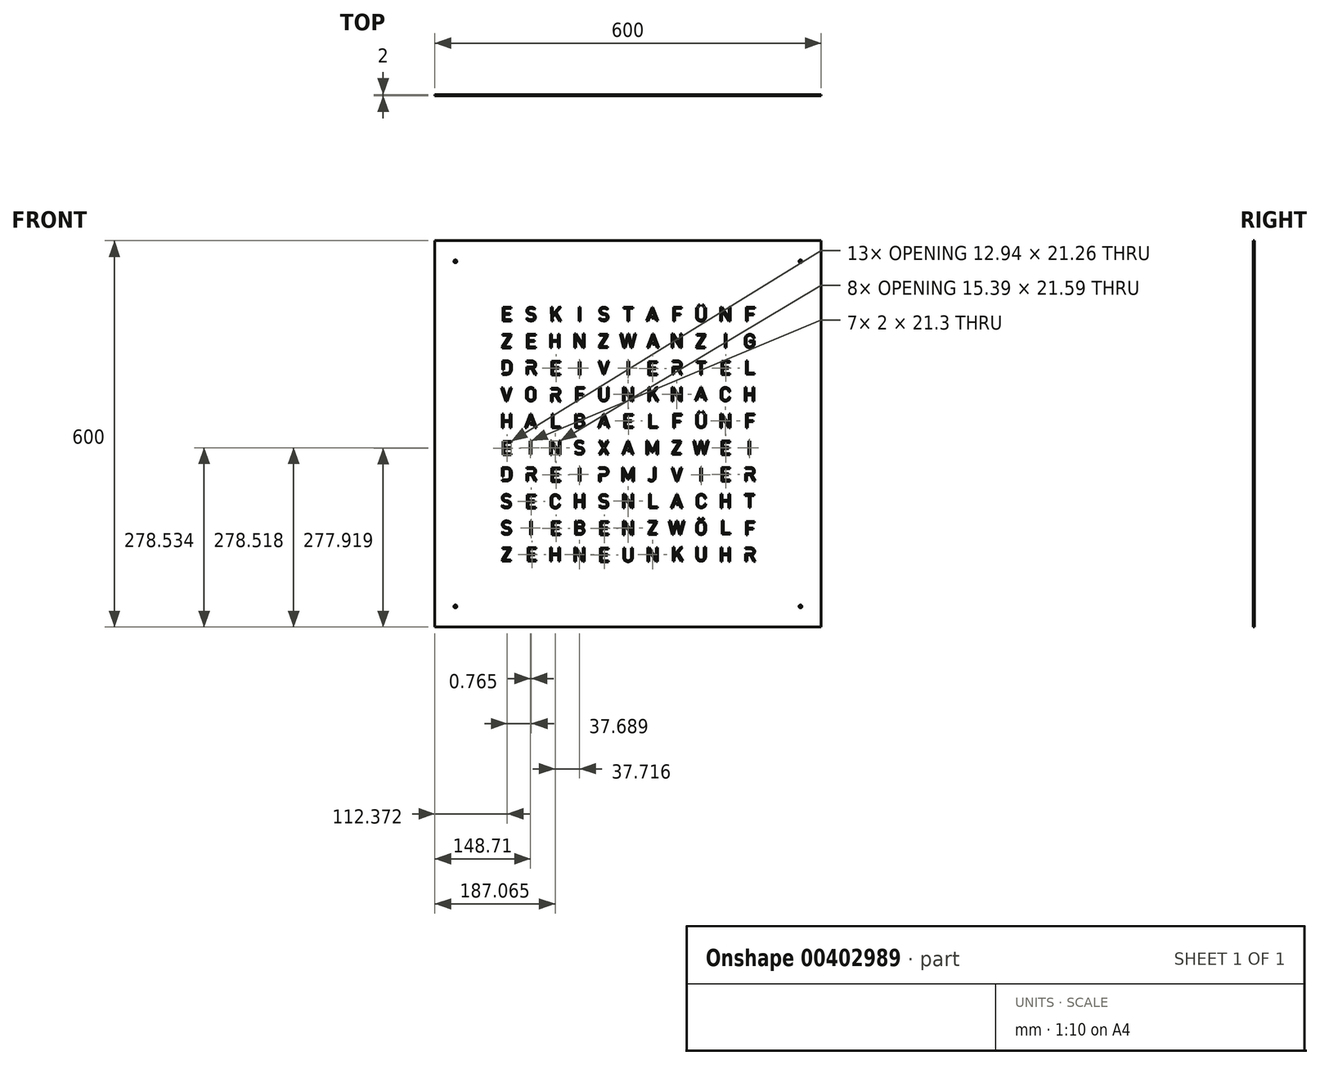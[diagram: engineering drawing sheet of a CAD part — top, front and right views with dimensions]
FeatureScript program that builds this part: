
annotation { "Feature Type Name" : "Feature", "Feature Type Description" : "" }
export const myFeature = defineFeature(function(context is Context, id is Id, definition is map)
    precondition{}
    {
        {
            var Q0;
            Q0=qCreatedBy(makeId("Front.planeOp"),FACE);
            var sketch = newSketch(context, id + "F0", { "sketchPlane" : qUnion([Q0])});
            skLineSegment(sketch, "E0.bottom", {"start": v(-458.3, 400.46) * mm, "end": v(141.7, 400.46) * mm});
            skLineSegment(sketch, "E0.top", {"start": v(-458.3, -199.54) * mm, "end": v(141.7, -199.54) * mm});
            skLineSegment(sketch, "E0.left", {"start": v(-458.3, 400.46) * mm, "end": v(-458.3, -199.54) * mm});
            skLineSegment(sketch, "E0.right", {"start": v(141.7, 400.46) * mm, "end": v(141.7, -199.54) * mm});
            skLineSegment(sketch, "E1", {"start": v(-354.69, 171.84) * mm, "end": v(-347.74, 151.15) * mm});
            skLineSegment(sketch, "E2", {"start": v(-347.74, 151.15) * mm, "end": v(-345.77, 151.15) * mm});
            skLineSegment(sketch, "E3", {"start": v(-345.77, 151.15) * mm, "end": v(-338.81, 171.84) * mm});
            skLineSegment(sketch, "E4", {"start": v(-338.81, 171.84) * mm, "end": v(-340.92, 171.84) * mm});
            skLineSegment(sketch, "E5", {"start": v(-340.92, 171.84) * mm, "end": v(-346.75, 154.5) * mm});
            skPoint(sketch, "E5.endSnap0", {"position": v(-346.75, 151.15) * mm});
            skLineSegment(sketch, "E6", {"start": v(-346.75, 154.5) * mm, "end": v(-352.58, 171.84) * mm});
            skLineSegment(sketch, "E7", {"start": v(-352.58, 171.84) * mm, "end": v(-354.69, 171.84) * mm});
            skArc(sketch, "E8", {"start": v(-268.37, 161.99) * mm, "mid": v(-265.4, 166.18) * mm, "end": v(-269.23, 169.6) * mm});
            skArc(sketch, "E9", {"start": v(-268.17, 159.99) * mm, "mid": v(-263.4, 166.28) * mm, "end": v(-269.23, 171.6) * mm});
            skLineSegment(sketch, "E10", {"start": v(-269.23, 171.6) * mm, "end": v(-277.66, 171.6) * mm});
            skLineSegment(sketch, "E11", {"start": v(-277.66, 171.6) * mm, "end": v(-277.66, 169.6) * mm});
            skLineSegment(sketch, "E12", {"start": v(-277.66, 169.6) * mm, "end": v(-269.23, 169.6) * mm});
            skLineSegment(sketch, "E13", {"start": v(-268.37, 161.99) * mm, "end": v(-277.66, 161.99) * mm});
            skLineSegment(sketch, "E14", {"start": v(-277.66, 161.99) * mm, "end": v(-277.66, 150.6) * mm});
            skLineSegment(sketch, "E15", {"start": v(-277.66, 150.6) * mm, "end": v(-275.66, 150.6) * mm});
            skLineSegment(sketch, "E16", {"start": v(-275.66, 150.6) * mm, "end": v(-275.66, 159.99) * mm});
            skLineSegment(sketch, "E17", {"start": v(-275.66, 159.99) * mm, "end": v(-270.17, 159.99) * mm});
            skLineSegment(sketch, "E18", {"start": v(-270.17, 159.99) * mm, "end": v(-264.9, 150.46) * mm});
            skLineSegment(sketch, "E19", {"start": v(-264.9, 150.46) * mm, "end": v(-262.62, 150.46) * mm});
            skLineSegment(sketch, "E20", {"start": v(-262.62, 150.46) * mm, "end": v(-268.17, 159.99) * mm});
            skLineSegment(sketch, "E21", {"start": v(-314.37, 157.95) * mm, "end": v(-314.37, 165.71) * mm});
            skLineSegment(sketch, "E22", {"start": v(-303.94, 165.71) * mm, "end": v(-303.94, 157.95) * mm});
            skArc(sketch, "E23", {"start": v(-314.37, 165.71) * mm, "mid": v(-311.31, 170.45) * mm, "end": v(-305.73, 169.61) * mm});
            skLineSegment(sketch, "E24", {"start": v(-316.37, 165.71) * mm, "end": v(-316.37, 157.95) * mm});
            skLineSegment(sketch, "E25", {"start": v(-301.94, 165.71) * mm, "end": v(-301.94, 157.95) * mm});
            skArc(sketch, "E26", {"start": v(-316.37, 165.71) * mm, "mid": v(-312.26, 172.13) * mm, "end": v(-304.71, 171.08) * mm});
            skArc(sketch, "E27", {"start": v(-301.94, 165.71) * mm, "mid": v(-302.34, 167.92) * mm, "end": v(-303.48, 169.85) * mm});
            skArc(sketch, "E28", {"start": v(-303.94, 165.71) * mm, "mid": v(-304.14, 167.02) * mm, "end": v(-304.71, 168.22) * mm});
            skArc(sketch, "E29", {"start": v(-301.94, 157.95) * mm, "mid": v(-306.07, 151.6) * mm, "end": v(-313.54, 152.82) * mm});
            skArc(sketch, "E30", {"start": v(-303.94, 157.95) * mm, "mid": v(-307.03, 153.38) * mm, "end": v(-312.42, 154.52) * mm});
            skArc(sketch, "E31", {"start": v(-316.37, 157.95) * mm, "mid": v(-315.98, 155.78) * mm, "end": v(-314.87, 153.88) * mm});
            skArc(sketch, "E32", {"start": v(-314.37, 157.95) * mm, "mid": v(-314.19, 156.7) * mm, "end": v(-313.65, 155.57) * mm});
            skLineSegment(sketch, "E33", {"start": v(-305.73, 169.61) * mm, "end": v(-304.71, 171.08) * mm});
            skLineSegment(sketch, "E34", {"start": v(-304.71, 168.22) * mm, "end": v(-303.48, 169.85) * mm});
            skLineSegment(sketch, "E35", {"start": v(-313.65, 155.57) * mm, "end": v(-314.87, 153.88) * mm});
            skLineSegment(sketch, "E36", {"start": v(-312.42, 154.52) * mm, "end": v(-313.54, 152.82) * mm});
            skLineSegment(sketch, "E37", {"start": v(-353.9, 109.8) * mm, "end": v(-353.9, 131.18) * mm});
            skLineSegment(sketch, "E38", {"start": v(-353.9, 131.18) * mm, "end": v(-351.9, 131.18) * mm});
            skLineSegment(sketch, "E39", {"start": v(-351.9, 131.18) * mm, "end": v(-351.9, 121.51) * mm});
            skLineSegment(sketch, "E40", {"start": v(-351.9, 121.51) * mm, "end": v(-341.7, 121.51) * mm});
            skLineSegment(sketch, "E41", {"start": v(-341.7, 121.51) * mm, "end": v(-341.7, 131.18) * mm});
            skLineSegment(sketch, "E42", {"start": v(-341.7, 131.18) * mm, "end": v(-339.7, 131.18) * mm});
            skLineSegment(sketch, "E43", {"start": v(-339.7, 131.18) * mm, "end": v(-339.7, 109.8) * mm});
            skLineSegment(sketch, "E44", {"start": v(-339.7, 109.8) * mm, "end": v(-341.7, 109.8) * mm});
            skLineSegment(sketch, "E45", {"start": v(-341.7, 109.8) * mm, "end": v(-341.7, 119.51) * mm});
            skLineSegment(sketch, "E46", {"start": v(-341.7, 119.51) * mm, "end": v(-351.9, 119.51) * mm});
            skLineSegment(sketch, "E47", {"start": v(-351.9, 119.51) * mm, "end": v(-351.9, 109.8) * mm});
            skLineSegment(sketch, "E48", {"start": v(-351.9, 109.8) * mm, "end": v(-353.9, 109.8) * mm});
            skLineSegment(sketch, "E49", {"start": v(-317.92, 109.8) * mm, "end": v(-309.5, 131.18) * mm});
            skLineSegment(sketch, "E50", {"start": v(-309.5, 131.18) * mm, "end": v(-308.57, 131.18) * mm});
            skLineSegment(sketch, "E51", {"start": v(-308.57, 131.18) * mm, "end": v(-300.43, 109.8) * mm});
            skLineSegment(sketch, "E52", {"start": v(-300.43, 109.8) * mm, "end": v(-302.67, 109.8) * mm});
            skLineSegment(sketch, "E53", {"start": v(-302.67, 109.8) * mm, "end": v(-304.7, 115.11) * mm});
            skLineSegment(sketch, "E54", {"start": v(-304.7, 115.11) * mm, "end": v(-309.74, 115.11) * mm});
            skLineSegment(sketch, "E55", {"start": v(-309.74, 115.11) * mm, "end": v(-309.74, 117.11) * mm});
            skLineSegment(sketch, "E56", {"start": v(-309.74, 117.11) * mm, "end": v(-305.35, 117.11) * mm});
            skLineSegment(sketch, "E57", {"start": v(-305.35, 117.11) * mm, "end": v(-309.06, 126.85) * mm});
            skLineSegment(sketch, "E58", {"start": v(-309.06, 126.85) * mm, "end": v(-315.77, 109.8) * mm});
            skLineSegment(sketch, "E59", {"start": v(-315.77, 109.8) * mm, "end": v(-317.92, 109.8) * mm});
            skLineSegment(sketch, "E60", {"start": v(-276.46, 109.8) * mm, "end": v(-263.54, 109.8) * mm});
            skLineSegment(sketch, "E61", {"start": v(-263.54, 109.8) * mm, "end": v(-263.54, 111.8) * mm});
            skLineSegment(sketch, "E62", {"start": v(-263.54, 111.8) * mm, "end": v(-274.46, 111.8) * mm});
            skLineSegment(sketch, "E63", {"start": v(-274.46, 111.8) * mm, "end": v(-274.46, 131.18) * mm});
            skLineSegment(sketch, "E64", {"start": v(-274.46, 131.18) * mm, "end": v(-276.46, 131.18) * mm});
            skLineSegment(sketch, "E65", {"start": v(-276.46, 131.18) * mm, "end": v(-276.46, 109.8) * mm});
            skLineSegment(sketch, "E66", {"start": v(-239, 151.18) * mm, "end": v(-239, 172.67) * mm});
            skLineSegment(sketch, "E67", {"start": v(-239, 172.67) * mm, "end": v(-225.94, 172.67) * mm});
            skLineSegment(sketch, "E68", {"start": v(-225.94, 172.67) * mm, "end": v(-225.94, 170.67) * mm});
            skLineSegment(sketch, "E69", {"start": v(-225.94, 170.67) * mm, "end": v(-237, 170.67) * mm});
            skLineSegment(sketch, "E70", {"start": v(-237, 170.67) * mm, "end": v(-237, 162.42) * mm});
            skLineSegment(sketch, "E71", {"start": v(-237, 162.42) * mm, "end": v(-227.82, 162.42) * mm});
            skLineSegment(sketch, "E72", {"start": v(-227.82, 162.42) * mm, "end": v(-227.82, 160.42) * mm});
            skLineSegment(sketch, "E73", {"start": v(-227.82, 160.42) * mm, "end": v(-237, 160.42) * mm});
            skLineSegment(sketch, "E74", {"start": v(-237, 160.42) * mm, "end": v(-237, 151.18) * mm});
            skLineSegment(sketch, "E75", {"start": v(-237, 151.18) * mm, "end": v(-239, 151.18) * mm});
            skLineSegment(sketch, "E76", {"start": v(-202.89, 172.67) * mm, "end": v(-202.89, 157.96) * mm});
            skLineSegment(sketch, "E77", {"start": v(-200.89, 172.67) * mm, "end": v(-200.89, 157.96) * mm});
            skLineSegment(sketch, "E78", {"start": v(-202.89, 172.67) * mm, "end": v(-200.89, 172.67) * mm});
            skLineSegment(sketch, "E79", {"start": v(-190.7, 172.67) * mm, "end": v(-190.7, 157.96) * mm});
            skLineSegment(sketch, "E80", {"start": v(-188.7, 172.67) * mm, "end": v(-188.7, 157.96) * mm});
            skLineSegment(sketch, "E81", {"start": v(-190.7, 172.67) * mm, "end": v(-188.7, 172.67) * mm});
            skArc(sketch, "E82", {"start": v(-200.89, 157.96) * mm, "mid": v(-195.8, 152.87) * mm, "end": v(-190.7, 157.96) * mm});
            skArc(sketch, "E83", {"start": v(-202.89, 157.96) * mm, "mid": v(-195.8, 150.87) * mm, "end": v(-188.7, 157.96) * mm});
            skLineSegment(sketch, "E84", {"start": v(-165.7, 172.67) * mm, "end": v(-165.7, 151.08) * mm});
            skLineSegment(sketch, "E85", {"start": v(-165.7, 151.08) * mm, "end": v(-163.7, 151.08) * mm});
            skLineSegment(sketch, "E86", {"start": v(-163.7, 151.08) * mm, "end": v(-163.7, 168.95) * mm});
            skLineSegment(sketch, "E87", {"start": v(-163.7, 168.95) * mm, "end": v(-152.3, 151.08) * mm});
            skLineSegment(sketch, "E88", {"start": v(-152.3, 151.08) * mm, "end": v(-150.3, 151.08) * mm});
            skLineSegment(sketch, "E89", {"start": v(-150.3, 151.08) * mm, "end": v(-150.3, 172.67) * mm});
            skLineSegment(sketch, "E90", {"start": v(-150.3, 172.67) * mm, "end": v(-152.3, 172.67) * mm});
            skLineSegment(sketch, "E91", {"start": v(-152.3, 172.67) * mm, "end": v(-152.3, 154.8) * mm});
            skLineSegment(sketch, "E92", {"start": v(-152.3, 154.8) * mm, "end": v(-163.7, 172.67) * mm});
            skLineSegment(sketch, "E93", {"start": v(-163.7, 172.67) * mm, "end": v(-165.7, 172.67) * mm});
            skLineSegment(sketch, "E94", {"start": v(-126.4, 151.08) * mm, "end": v(-126.4, 172.67) * mm});
            skLineSegment(sketch, "E95", {"start": v(-126.4, 172.67) * mm, "end": v(-124.4, 172.67) * mm});
            skLineSegment(sketch, "E96", {"start": v(-124.4, 172.67) * mm, "end": v(-124.4, 160.57) * mm});
            skLineSegment(sketch, "E97", {"start": v(-124.4, 160.57) * mm, "end": v(-114.36, 172.67) * mm});
            skLineSegment(sketch, "E98", {"start": v(-114.36, 172.67) * mm, "end": v(-111.76, 172.67) * mm});
            skLineSegment(sketch, "E99", {"start": v(-111.76, 172.67) * mm, "end": v(-118.9, 164.06) * mm});
            skLineSegment(sketch, "E100", {"start": v(-118.9, 164.06) * mm, "end": v(-111.2, 151.08) * mm});
            skLineSegment(sketch, "E101", {"start": v(-111.2, 151.08) * mm, "end": v(-113.53, 151.08) * mm});
            skLineSegment(sketch, "E102", {"start": v(-113.53, 151.08) * mm, "end": v(-120.18, 162.28) * mm});
            skLineSegment(sketch, "E103", {"start": v(-120.18, 162.28) * mm, "end": v(-124.4, 157.19) * mm});
            skLineSegment(sketch, "E104", {"start": v(-124.4, 157.19) * mm, "end": v(-124.4, 151.08) * mm});
            skLineSegment(sketch, "E105", {"start": v(-124.4, 151.08) * mm, "end": v(-126.4, 151.08) * mm});
            skLineSegment(sketch, "E106", {"start": v(-12.14, 165.54) * mm, "end": v(-12.14, 158.4) * mm});
            skLineSegment(sketch, "E107", {"start": v(-14.14, 158.4) * mm, "end": v(-14.14, 165.54) * mm});
            skArc(sketch, "E108", {"start": v(-12.14, 165.54) * mm, "mid": v(-7.1, 170.78) * mm, "end": v(-1.67, 165.93) * mm});
            skArc(sketch, "E109", {"start": v(-14.14, 165.54) * mm, "mid": v(-7.1, 172.78) * mm, "end": v(0.33, 165.93) * mm});
            skArc(sketch, "E110", {"start": v(-12.14, 158.4) * mm, "mid": v(-7.2, 153.16) * mm, "end": v(-1.67, 157.75) * mm});
            skArc(sketch, "E111", {"start": v(-14.14, 158.4) * mm, "mid": v(-7.21, 151.16) * mm, "end": v(0.33, 157.75) * mm});
            skLineSegment(sketch, "E112", {"start": v(-1.67, 157.75) * mm, "end": v(0.33, 157.75) * mm});
            skLineSegment(sketch, "E113", {"start": v(-1.67, 165.93) * mm, "end": v(0.33, 165.93) * mm});
            skLineSegment(sketch, "E114", {"start": v(-163.64, 130.95) * mm, "end": v(-150.7, 130.95) * mm});
            skLineSegment(sketch, "E115", {"start": v(-150.7, 130.95) * mm, "end": v(-150.7, 128.95) * mm});
            skLineSegment(sketch, "E116", {"start": v(-150.7, 128.95) * mm, "end": v(-161.64, 128.95) * mm});
            skLineSegment(sketch, "E117", {"start": v(-161.64, 128.95) * mm, "end": v(-161.64, 121.44) * mm});
            skLineSegment(sketch, "E118", {"start": v(-161.64, 121.44) * mm, "end": v(-152.42, 121.44) * mm});
            skLineSegment(sketch, "E119", {"start": v(-152.42, 121.44) * mm, "end": v(-152.42, 119.44) * mm});
            skLineSegment(sketch, "E120", {"start": v(-152.42, 119.44) * mm, "end": v(-161.64, 119.44) * mm});
            skLineSegment(sketch, "E121", {"start": v(-161.64, 119.44) * mm, "end": v(-161.64, 111.7) * mm});
            skLineSegment(sketch, "E122", {"start": v(-161.64, 111.7) * mm, "end": v(-150.7, 111.7) * mm});
            skLineSegment(sketch, "E123", {"start": v(-150.7, 111.7) * mm, "end": v(-150.7, 109.7) * mm});
            skLineSegment(sketch, "E124", {"start": v(-150.7, 109.7) * mm, "end": v(-163.64, 109.7) * mm});
            skLineSegment(sketch, "E125", {"start": v(-163.64, 109.7) * mm, "end": v(-163.64, 130.95) * mm});
            skLineSegment(sketch, "E126", {"start": v(-240.27, 130.88) * mm, "end": v(-238.27, 130.88) * mm});
            skLineSegment(sketch, "E127", {"start": v(-238.27, 130.88) * mm, "end": v(-238.27, 111.92) * mm});
            skLineSegment(sketch, "E128", {"start": v(-238.27, 111.92) * mm, "end": v(-232.05, 111.92) * mm});
            skLineSegment(sketch, "E129", {"start": v(-240.27, 130.88) * mm, "end": v(-240.27, 109.92) * mm});
            skLineSegment(sketch, "E130", {"start": v(-240.27, 109.92) * mm, "end": v(-232.05, 109.92) * mm});
            skArc(sketch, "E131", {"start": v(-232.05, 111.92) * mm, "mid": v(-228.06, 115.9) * mm, "end": v(-232.05, 119.9) * mm});
            skArc(sketch, "E132", {"start": v(-232.05, 109.92) * mm, "mid": v(-226.37, 114.28) * mm, "end": v(-229.11, 120.88) * mm});
            skLineSegment(sketch, "E133", {"start": v(-232.05, 119.9) * mm, "end": v(-235.96, 119.9) * mm});
            skLineSegment(sketch, "E134", {"start": v(-235.96, 119.9) * mm, "end": v(-235.96, 121.9) * mm});
            skLineSegment(sketch, "E135", {"start": v(-235.96, 121.9) * mm, "end": v(-232.05, 121.9) * mm});
            skArc(sketch, "E136", {"start": v(-232.05, 121.9) * mm, "mid": v(-228.55, 125.39) * mm, "end": v(-232.05, 128.88) * mm});
            skLineSegment(sketch, "E137", {"start": v(-232.05, 128.88) * mm, "end": v(-235.96, 128.88) * mm});
            skLineSegment(sketch, "E138", {"start": v(-235.96, 128.88) * mm, "end": v(-235.96, 130.88) * mm});
            skLineSegment(sketch, "E139", {"start": v(-235.96, 130.88) * mm, "end": v(-232.05, 130.88) * mm});
            skArc(sketch, "E140", {"start": v(-232.05, 130.88) * mm, "mid": v(-226.84, 126.98) * mm, "end": v(-229.11, 120.88) * mm});
            skLineSegment(sketch, "E141", {"start": v(-310.6, 68.33) * mm, "end": v(-310.6, 89.63) * mm});
            skLineSegment(sketch, "E142", {"start": v(-310.6, 89.63) * mm, "end": v(-308.6, 89.63) * mm});
            skLineSegment(sketch, "E143", {"start": v(-308.6, 89.63) * mm, "end": v(-308.6, 68.33) * mm});
            skLineSegment(sketch, "E144", {"start": v(-308.6, 68.33) * mm, "end": v(-310.6, 68.33) * mm});
            skLineSegment(sketch, "E145", {"start": v(-202.92, 89.54) * mm, "end": v(-200.6, 89.54) * mm});
            skLineSegment(sketch, "E146", {"start": v(-200.6, 89.54) * mm, "end": v(-195.8, 81.48) * mm});
            skLineSegment(sketch, "E147", {"start": v(-195.8, 81.48) * mm, "end": v(-191, 89.54) * mm});
            skLineSegment(sketch, "E148", {"start": v(-191, 89.54) * mm, "end": v(-188.66, 89.54) * mm});
            skLineSegment(sketch, "E149", {"start": v(-188.66, 89.54) * mm, "end": v(-194.99, 78.93) * mm});
            skLineSegment(sketch, "E150", {"start": v(-194.99, 78.93) * mm, "end": v(-188.66, 68.33) * mm});
            skLineSegment(sketch, "E151", {"start": v(-188.66, 68.33) * mm, "end": v(-191, 68.33) * mm});
            skLineSegment(sketch, "E152", {"start": v(-191, 68.33) * mm, "end": v(-195.8, 76.38) * mm});
            skLineSegment(sketch, "E153", {"start": v(-195.8, 76.38) * mm, "end": v(-200.6, 68.33) * mm});
            skLineSegment(sketch, "E154", {"start": v(-200.6, 68.33) * mm, "end": v(-202.92, 68.33) * mm});
            skLineSegment(sketch, "E155", {"start": v(-202.92, 68.33) * mm, "end": v(-196.6, 78.93) * mm});
            skLineSegment(sketch, "E156", {"start": v(-196.6, 78.93) * mm, "end": v(-202.92, 89.54) * mm});
            skLineSegment(sketch, "E157", {"start": v(-129.2, 68.4) * mm, "end": v(-129.2, 89.73) * mm});
            skLineSegment(sketch, "E158", {"start": v(-129.2, 89.73) * mm, "end": v(-127.72, 89.73) * mm});
            skLineSegment(sketch, "E159", {"start": v(-127.72, 89.73) * mm, "end": v(-120.22, 74.46) * mm});
            skLineSegment(sketch, "E160", {"start": v(-120.22, 74.46) * mm, "end": v(-113.2, 89.73) * mm});
            skLineSegment(sketch, "E161", {"start": v(-113.2, 89.73) * mm, "end": v(-111.57, 89.73) * mm});
            skLineSegment(sketch, "E162", {"start": v(-111.57, 89.73) * mm, "end": v(-111.57, 68.4) * mm});
            skLineSegment(sketch, "E163", {"start": v(-111.57, 68.4) * mm, "end": v(-113.57, 68.4) * mm});
            skLineSegment(sketch, "E164", {"start": v(-113.57, 68.4) * mm, "end": v(-113.57, 84.14) * mm});
            skLineSegment(sketch, "E165", {"start": v(-113.57, 84.14) * mm, "end": v(-119.35, 71.56) * mm});
            skLineSegment(sketch, "E166", {"start": v(-119.35, 71.56) * mm, "end": v(-121.03, 71.56) * mm});
            skLineSegment(sketch, "E167", {"start": v(-121.03, 71.56) * mm, "end": v(-127.2, 84.14) * mm});
            skLineSegment(sketch, "E168", {"start": v(-127.2, 84.14) * mm, "end": v(-127.2, 68.4) * mm});
            skLineSegment(sketch, "E169", {"start": v(-127.2, 68.4) * mm, "end": v(-129.2, 68.4) * mm});
            skLineSegment(sketch, "E170", {"start": v(-75.93, 68.4) * mm, "end": v(-89.16, 68.4) * mm});
            skLineSegment(sketch, "E171", {"start": v(-89.16, 68.4) * mm, "end": v(-89.16, 70.4) * mm});
            skLineSegment(sketch, "E172", {"start": v(-89.16, 70.4) * mm, "end": v(-78.86, 86.66) * mm});
            skLineSegment(sketch, "E173", {"start": v(-78.86, 86.66) * mm, "end": v(-78.86, 87.47) * mm});
            skLineSegment(sketch, "E174", {"start": v(-78.86, 87.47) * mm, "end": v(-88.64, 87.47) * mm});
            skLineSegment(sketch, "E175", {"start": v(-88.64, 87.47) * mm, "end": v(-88.64, 89.47) * mm});
            skLineSegment(sketch, "E176", {"start": v(-88.64, 89.47) * mm, "end": v(-75.99, 89.47) * mm});
            skLineSegment(sketch, "E177", {"start": v(-75.99, 89.47) * mm, "end": v(-75.99, 87.47) * mm});
            skLineSegment(sketch, "E178", {"start": v(-75.99, 87.47) * mm, "end": v(-86.79, 70.4) * mm});
            skLineSegment(sketch, "E179", {"start": v(-86.79, 70.4) * mm, "end": v(-75.93, 70.4) * mm});
            skLineSegment(sketch, "E180", {"start": v(-75.93, 70.4) * mm, "end": v(-75.93, 68.4) * mm});
            skLineSegment(sketch, "E181", {"start": v(-56.7, 89.47) * mm, "end": v(-54.64, 89.47) * mm});
            skLineSegment(sketch, "E182", {"start": v(-54.64, 89.47) * mm, "end": v(-50.62, 72.62) * mm});
            skLineSegment(sketch, "E183", {"start": v(-50.62, 72.62) * mm, "end": v(-45.49, 89.47) * mm});
            skLineSegment(sketch, "E184", {"start": v(-45.49, 89.47) * mm, "end": v(-43.88, 89.47) * mm});
            skLineSegment(sketch, "E185", {"start": v(-43.88, 89.47) * mm, "end": v(-39.46, 72.62) * mm});
            skLineSegment(sketch, "E186", {"start": v(-39.46, 72.62) * mm, "end": v(-35.18, 89.47) * mm});
            skLineSegment(sketch, "E187", {"start": v(-35.18, 89.47) * mm, "end": v(-33.12, 89.47) * mm});
            skLineSegment(sketch, "E188", {"start": v(-33.12, 89.47) * mm, "end": v(-38.42, 68.59) * mm});
            skLineSegment(sketch, "E189", {"start": v(-38.42, 68.59) * mm, "end": v(-40.47, 68.59) * mm});
            skLineSegment(sketch, "E190", {"start": v(-40.47, 68.59) * mm, "end": v(-44.77, 84.97) * mm});
            skLineSegment(sketch, "E191", {"start": v(-44.77, 84.97) * mm, "end": v(-49.76, 68.59) * mm});
            skLineSegment(sketch, "E192", {"start": v(-49.76, 68.59) * mm, "end": v(-51.72, 68.59) * mm});
            skLineSegment(sketch, "E193", {"start": v(-51.72, 68.59) * mm, "end": v(-56.7, 89.47) * mm});
            skLineSegment(sketch, "E194", {"start": v(-353.56, 34.3) * mm, "end": v(-353.56, 48.11) * mm});
            skLineSegment(sketch, "E195", {"start": v(-353.56, 48.11) * mm, "end": v(-345.99, 48.11) * mm});
            skLineSegment(sketch, "E196", {"start": v(-353.56, 34.3) * mm, "end": v(-351.56, 34.3) * mm});
            skLineSegment(sketch, "E197", {"start": v(-351.56, 34.3) * mm, "end": v(-351.56, 46.11) * mm});
            skLineSegment(sketch, "E198", {"start": v(-351.56, 46.11) * mm, "end": v(-345.99, 46.11) * mm});
            skLineSegment(sketch, "E199", {"start": v(-353.56, 29.12) * mm, "end": v(-353.56, 26.98) * mm});
            skLineSegment(sketch, "E200", {"start": v(-353.56, 26.98) * mm, "end": v(-346.65, 26.98) * mm});
            skLineSegment(sketch, "E201", {"start": v(-353.56, 29.12) * mm, "end": v(-346.65, 29.12) * mm});
            skArc(sketch, "E202", {"start": v(-345.99, 46.11) * mm, "mid": v(-342.73, 44.8) * mm, "end": v(-341.3, 41.6) * mm});
            skArc(sketch, "E203", {"start": v(-345.99, 48.11) * mm, "mid": v(-341.32, 46.22) * mm, "end": v(-339.3, 41.6) * mm});
            skArc(sketch, "E204", {"start": v(-346.65, 29.12) * mm, "mid": v(-342.93, 30.62) * mm, "end": v(-341.3, 34.3) * mm});
            skArc(sketch, "E205", {"start": v(-346.65, 26.98) * mm, "mid": v(-341.46, 29.12) * mm, "end": v(-339.3, 34.3) * mm});
            skLineSegment(sketch, "E206", {"start": v(-341.3, 41.6) * mm, "end": v(-341.3, 34.3) * mm});
            skLineSegment(sketch, "E207", {"start": v(-339.3, 41.6) * mm, "end": v(-339.3, 34.3) * mm});
            skLineSegment(sketch, "E208", {"start": v(-202.82, 26.82) * mm, "end": v(-200.82, 26.82) * mm});
            skLineSegment(sketch, "E209", {"start": v(-200.82, 26.82) * mm, "end": v(-200.82, 35.5) * mm});
            skLineSegment(sketch, "E210", {"start": v(-200.82, 35.5) * mm, "end": v(-194.9, 35.5) * mm});
            skLineSegment(sketch, "E211", {"start": v(-202.82, 26.82) * mm, "end": v(-202.82, 37.5) * mm});
            skLineSegment(sketch, "E212", {"start": v(-202.82, 37.5) * mm, "end": v(-194.9, 37.5) * mm});
            skLineSegment(sketch, "E213", {"start": v(-202.82, 46.16) * mm, "end": v(-202.82, 48.16) * mm});
            skLineSegment(sketch, "E214", {"start": v(-202.82, 48.16) * mm, "end": v(-194.9, 48.16) * mm});
            skLineSegment(sketch, "E215", {"start": v(-202.82, 46.16) * mm, "end": v(-194.9, 46.16) * mm});
            skArc(sketch, "E216", {"start": v(-194.9, 37.5) * mm, "mid": v(-190.57, 41.84) * mm, "end": v(-194.9, 46.16) * mm});
            skArc(sketch, "E217", {"start": v(-194.9, 48.16) * mm, "mid": v(-188.57, 41.84) * mm, "end": v(-194.9, 35.5) * mm});
            skLineSegment(sketch, "E218", {"start": v(-117.73, 32.88) * mm, "end": v(-117.73, 48) * mm});
            skLineSegment(sketch, "E219", {"start": v(-117.73, 48) * mm, "end": v(-115.73, 48) * mm});
            skLineSegment(sketch, "E220", {"start": v(-115.73, 48) * mm, "end": v(-115.73, 32.88) * mm});
            skArc(sketch, "E221", {"start": v(-117.73, 32.88) * mm, "mid": v(-120.64, 28.88) * mm, "end": v(-125.35, 30.41) * mm});
            skArc(sketch, "E222", {"start": v(-115.73, 32.88) * mm, "mid": v(-119.85, 27.04) * mm, "end": v(-126.73, 28.97) * mm});
            skLineSegment(sketch, "E223", {"start": v(-126.73, 28.97) * mm, "end": v(-125.35, 30.41) * mm});
            skLineSegment(sketch, "E224", {"start": v(-235.24, 78.34) * mm, "end": v(-231.64, 77.65) * mm});
            skArc(sketch, "E225", {"start": v(-231.64, 77.65) * mm, "mid": v(-228.68, 73.76) * mm, "end": v(-232.23, 70.4) * mm});
            skLineSegment(sketch, "E226", {"start": v(-235.64, 80.45) * mm, "end": v(-231.18, 79.6) * mm});
            skArc(sketch, "E227", {"start": v(-231.18, 79.6) * mm, "mid": v(-226.6, 73.6) * mm, "end": v(-232.09, 68.4) * mm});
            skLineSegment(sketch, "E228", {"start": v(-232.23, 70.4) * mm, "end": v(-234.2, 70.35) * mm});
            skLineSegment(sketch, "E229", {"start": v(-232.09, 68.4) * mm, "end": v(-234.2, 68.35) * mm});
            skArc(sketch, "E230", {"start": v(-234.2, 70.35) * mm, "mid": v(-237.1, 70.94) * mm, "end": v(-239.45, 72.73) * mm});
            skArc(sketch, "E231", {"start": v(-234.2, 68.35) * mm, "mid": v(-237.88, 69.09) * mm, "end": v(-240.89, 71.34) * mm});
            skLineSegment(sketch, "E232", {"start": v(-240.89, 71.34) * mm, "end": v(-239.45, 72.73) * mm});
            skLineSegment(sketch, "E233", {"start": v(-228.8, 85.68) * mm, "end": v(-227.3, 87.02) * mm});
            skLineSegment(sketch, "E234", {"start": v(-234.55, 89.8) * mm, "end": v(-233.11, 89.8) * mm});
            skLineSegment(sketch, "E235", {"start": v(-234.48, 87.8) * mm, "end": v(-233.18, 87.8) * mm});
            skArc(sketch, "E236", {"start": v(-233.11, 89.8) * mm, "mid": v(-229.9, 89.07) * mm, "end": v(-227.3, 87.02) * mm});
            skArc(sketch, "E237", {"start": v(-233.18, 87.8) * mm, "mid": v(-230.74, 87.25) * mm, "end": v(-228.8, 85.68) * mm});
            skArc(sketch, "E238", {"start": v(-234.48, 87.8) * mm, "mid": v(-238.2, 84.62) * mm, "end": v(-235.64, 80.45) * mm});
            skArc(sketch, "E239", {"start": v(-234.55, 89.8) * mm, "mid": v(-240.3, 84.4) * mm, "end": v(-235.24, 78.34) * mm});
            skLineSegment(sketch, "E240", {"start": v(29.78, -14.12) * mm, "end": v(31.78, -14.12) * mm});
            skLineSegment(sketch, "E241", {"start": v(31.78, -14.12) * mm, "end": v(31.78, 4.74) * mm});
            skLineSegment(sketch, "E242", {"start": v(31.78, 4.74) * mm, "end": v(37.8, 4.74) * mm});
            skLineSegment(sketch, "E243", {"start": v(37.8, 4.74) * mm, "end": v(37.8, 6.74) * mm});
            skLineSegment(sketch, "E244", {"start": v(37.8, 6.74) * mm, "end": v(23.75, 6.74) * mm});
            skLineSegment(sketch, "E245", {"start": v(23.75, 6.74) * mm, "end": v(23.75, 4.74) * mm});
            skLineSegment(sketch, "E246", {"start": v(23.75, 4.74) * mm, "end": v(29.78, 4.74) * mm});
            skLineSegment(sketch, "E247", {"start": v(29.78, 4.74) * mm, "end": v(29.78, -14.12) * mm});
            skLineSegment(sketch, "E248", {"start": v(36.37, 243.22) * mm, "end": v(30.6, 243.22) * mm});
            skLineSegment(sketch, "E249", {"start": v(30.6, 243.22) * mm, "end": v(30.6, 245.22) * mm});
            skLineSegment(sketch, "E250", {"start": v(30.6, 245.22) * mm, "end": v(38.37, 245.22) * mm});
            skLineSegment(sketch, "E251", {"start": v(38.37, 245.22) * mm, "end": v(38.37, 241.26) * mm});
            skLineSegment(sketch, "E252", {"start": v(36.37, 243.22) * mm, "end": v(36.37, 241.26) * mm});
            skLineSegment(sketch, "E253", {"start": v(25.54, 247.9) * mm, "end": v(25.54, 241.26) * mm});
            skLineSegment(sketch, "E254", {"start": v(23.54, 247.9) * mm, "end": v(23.54, 241.26) * mm});
            skArc(sketch, "E255", {"start": v(25.54, 241.26) * mm, "mid": v(30.96, 235.85) * mm, "end": v(36.37, 241.26) * mm});
            skArc(sketch, "E256", {"start": v(23.54, 241.26) * mm, "mid": v(30.96, 233.85) * mm, "end": v(38.37, 241.26) * mm});
            skArc(sketch, "E257", {"start": v(25.54, 247.9) * mm, "mid": v(30.5, 253.34) * mm, "end": v(36.37, 248.91) * mm});
            skArc(sketch, "E258", {"start": v(23.54, 247.9) * mm, "mid": v(30.49, 255.33) * mm, "end": v(38.37, 248.91) * mm});
            skLineSegment(sketch, "E259", {"start": v(36.37, 248.91) * mm, "end": v(38.37, 248.91) * mm});
            skLineSegment(sketch, "E260.bottom", {"start": v(-48.6, 135.2) * mm, "end": v(-46.6, 135.2) * mm});
            skLineSegment(sketch, "E260.top", {"start": v(-48.6, 132.7) * mm, "end": v(-46.6, 132.7) * mm});
            skLineSegment(sketch, "E260.left", {"start": v(-48.6, 135.2) * mm, "end": v(-48.6, 132.7) * mm});
            skLineSegment(sketch, "E260.right", {"start": v(-46.6, 135.2) * mm, "end": v(-46.6, 132.7) * mm});
            skLineSegment(sketch, "E261.bottom", {"start": v(-42.55, 135.2) * mm, "end": v(-40.55, 135.2) * mm});
            skLineSegment(sketch, "E261.top", {"start": v(-42.55, 132.7) * mm, "end": v(-40.55, 132.7) * mm});
            skLineSegment(sketch, "E261.left", {"start": v(-42.55, 135.2) * mm, "end": v(-42.55, 132.7) * mm});
            skLineSegment(sketch, "E261.right", {"start": v(-40.55, 135.2) * mm, "end": v(-40.55, 132.7) * mm});
            skLineSegment(sketch, "E262", {"start": v(-51.95, 131.1) * mm, "end": v(-49.95, 131.1) * mm});
            skLineSegment(sketch, "E263", {"start": v(-49.95, 131.1) * mm, "end": v(-49.95, 116.95) * mm});
            skLineSegment(sketch, "E264", {"start": v(-51.95, 131.1) * mm, "end": v(-51.95, 116.95) * mm});
            skLineSegment(sketch, "E265", {"start": v(-39.43, 131.1) * mm, "end": v(-37.43, 131.1) * mm});
            skLineSegment(sketch, "E266", {"start": v(-37.43, 131.1) * mm, "end": v(-37.43, 116.95) * mm});
            skLineSegment(sketch, "E267", {"start": v(-39.43, 131.1) * mm, "end": v(-39.43, 116.95) * mm});
            skArc(sketch, "E268", {"start": v(-49.95, 116.95) * mm, "mid": v(-44.69, 111.69) * mm, "end": v(-39.43, 116.95) * mm});
            skArc(sketch, "E269", {"start": v(-51.95, 116.95) * mm, "mid": v(-44.69, 109.69) * mm, "end": v(-37.43, 116.95) * mm});
            skLineSegment(sketch, "E270.bottom", {"start": v(-48.73, -30.47) * mm, "end": v(-46.73, -30.47) * mm});
            skLineSegment(sketch, "E270.top", {"start": v(-48.73, -32.97) * mm, "end": v(-46.73, -32.97) * mm});
            skLineSegment(sketch, "E270.left", {"start": v(-48.73, -30.47) * mm, "end": v(-48.73, -32.97) * mm});
            skLineSegment(sketch, "E270.right", {"start": v(-46.73, -30.47) * mm, "end": v(-46.73, -32.97) * mm});
            skLineSegment(sketch, "E271.bottom", {"start": v(-42.8, -30.47) * mm, "end": v(-40.68, -30.47) * mm});
            skLineSegment(sketch, "E271.top", {"start": v(-42.8, -32.97) * mm, "end": v(-40.68, -32.97) * mm});
            skLineSegment(sketch, "E271.left", {"start": v(-42.8, -30.47) * mm, "end": v(-42.8, -32.97) * mm});
            skLineSegment(sketch, "E271.right", {"start": v(-40.68, -30.47) * mm, "end": v(-40.68, -32.97) * mm});
            skLineSegment(sketch, "E272", {"start": v(-51.91, -42.02) * mm, "end": v(-51.91, -49.08) * mm});
            skLineSegment(sketch, "E273", {"start": v(-49.91, -49.08) * mm, "end": v(-49.91, -42.02) * mm});
            skLineSegment(sketch, "E274", {"start": v(-39.6, -42.02) * mm, "end": v(-39.6, -49.08) * mm});
            skLineSegment(sketch, "E275", {"start": v(-37.6, -42.02) * mm, "end": v(-37.6, -49.08) * mm});
            skArc(sketch, "E276", {"start": v(-51.91, -42.02) * mm, "mid": v(-47.99, -35.52) * mm, "end": v(-40.4, -35.96) * mm});
            skArc(sketch, "E277", {"start": v(-49.91, -42.02) * mm, "mid": v(-47.03, -37.28) * mm, "end": v(-41.5, -37.63) * mm});
            skArc(sketch, "E278", {"start": v(-39.6, -42.02) * mm, "mid": v(-39.74, -40.61) * mm, "end": v(-40.11, -39.24) * mm});
            skArc(sketch, "E279", {"start": v(-37.6, -42.02) * mm, "mid": v(-37.97, -39.69) * mm, "end": v(-39.02, -37.57) * mm});
            skArc(sketch, "E280", {"start": v(-39.6, -49.08) * mm, "mid": v(-42.54, -53.75) * mm, "end": v(-48.02, -53.12) * mm});
            skArc(sketch, "E281", {"start": v(-37.6, -49.08) * mm, "mid": v(-41.6, -55.52) * mm, "end": v(-49.15, -54.77) * mm});
            skArc(sketch, "E282", {"start": v(-49.91, -49.08) * mm, "mid": v(-49.8, -50.42) * mm, "end": v(-49.5, -51.73) * mm});
            skArc(sketch, "E283", {"start": v(-51.91, -49.08) * mm, "mid": v(-51.55, -51.39) * mm, "end": v(-50.49, -53.46) * mm});
            skLineSegment(sketch, "E284", {"start": v(-41.5, -37.63) * mm, "end": v(-40.4, -35.96) * mm});
            skLineSegment(sketch, "E285", {"start": v(-40.11, -39.24) * mm, "end": v(-39.02, -37.57) * mm});
            skLineSegment(sketch, "E286", {"start": v(-49.5, -51.73) * mm, "end": v(-50.49, -53.46) * mm});
            skLineSegment(sketch, "E287", {"start": v(-49.15, -54.77) * mm, "end": v(-48.02, -53.12) * mm});
            skCircle(sketch, "E288", {"center": v(-426.3, 368.46) * mm, "radius": 2.36 * mm});
            skCircle(sketch, "E289", {"center": v(109.7, 368.46) * mm, "radius": 2.32 * mm});
            skCircle(sketch, "E290", {"center": v(-426.3, -167.54) * mm, "radius": 2.33 * mm});
            skCircle(sketch, "E291", {"center": v(109.7, -167.54) * mm, "radius": 2.27 * mm});
            skLineSegment(sketch, "E292", {"start": v(-314.82, 255.23) * mm, "end": v(-301.78, 255.23) * mm});
            skLineSegment(sketch, "E293", {"start": v(-301.78, 255.23) * mm, "end": v(-301.78, 253.23) * mm});
            skLineSegment(sketch, "E294", {"start": v(-301.78, 253.23) * mm, "end": v(-312.82, 253.23) * mm});
            skLineSegment(sketch, "E295", {"start": v(-312.82, 253.23) * mm, "end": v(-312.82, 245.58) * mm});
            skLineSegment(sketch, "E296", {"start": v(-312.82, 245.58) * mm, "end": v(-303.28, 245.58) * mm});
            skLineSegment(sketch, "E297", {"start": v(-303.28, 245.58) * mm, "end": v(-303.28, 243.58) * mm});
            skLineSegment(sketch, "E298", {"start": v(-303.28, 243.58) * mm, "end": v(-312.82, 243.58) * mm});
            skLineSegment(sketch, "E299", {"start": v(-312.82, 243.58) * mm, "end": v(-312.82, 235.73) * mm});
            skLineSegment(sketch, "E300", {"start": v(-312.82, 235.73) * mm, "end": v(-301.78, 235.73) * mm});
            skLineSegment(sketch, "E301", {"start": v(-301.78, 235.73) * mm, "end": v(-301.78, 233.73) * mm});
            skLineSegment(sketch, "E302", {"start": v(-301.78, 233.73) * mm, "end": v(-314.82, 233.73) * mm});
            skLineSegment(sketch, "E303", {"start": v(-314.82, 233.73) * mm, "end": v(-314.82, 255.23) * mm});
            skLineSegment(sketch, "E304", {"start": v(-352.4, 89) * mm, "end": v(-339.46, 89) * mm});
            skLineSegment(sketch, "E305", {"start": v(-339.46, 89) * mm, "end": v(-339.46, 87) * mm});
            skLineSegment(sketch, "E306", {"start": v(-339.46, 87) * mm, "end": v(-350.4, 87) * mm});
            skLineSegment(sketch, "E307", {"start": v(-350.4, 87) * mm, "end": v(-350.4, 79.5) * mm});
            skLineSegment(sketch, "E308", {"start": v(-350.4, 79.5) * mm, "end": v(-341.18, 79.5) * mm});
            skLineSegment(sketch, "E309", {"start": v(-341.18, 79.5) * mm, "end": v(-341.18, 77.5) * mm});
            skLineSegment(sketch, "E310", {"start": v(-341.18, 77.5) * mm, "end": v(-350.4, 77.5) * mm});
            skLineSegment(sketch, "E311", {"start": v(-350.4, 77.5) * mm, "end": v(-350.4, 69.75) * mm});
            skLineSegment(sketch, "E312", {"start": v(-350.4, 69.75) * mm, "end": v(-339.46, 69.75) * mm});
            skLineSegment(sketch, "E313", {"start": v(-339.46, 69.75) * mm, "end": v(-339.46, 67.75) * mm});
            skLineSegment(sketch, "E314", {"start": v(-339.46, 67.75) * mm, "end": v(-352.4, 67.75) * mm});
            skLineSegment(sketch, "E315", {"start": v(-352.4, 67.75) * mm, "end": v(-352.4, 89) * mm});
            skLineSegment(sketch, "E316", {"start": v(-314.7, 6) * mm, "end": v(-301.77, 6) * mm});
            skLineSegment(sketch, "E317", {"start": v(-301.77, 6) * mm, "end": v(-301.77, 4) * mm});
            skLineSegment(sketch, "E318", {"start": v(-301.77, 4) * mm, "end": v(-312.7, 4) * mm});
            skLineSegment(sketch, "E319", {"start": v(-312.7, 4) * mm, "end": v(-312.7, -3.5) * mm});
            skLineSegment(sketch, "E320", {"start": v(-312.7, -3.5) * mm, "end": v(-303.5, -3.5) * mm});
            skLineSegment(sketch, "E321", {"start": v(-303.5, -3.5) * mm, "end": v(-303.5, -5.5) * mm});
            skLineSegment(sketch, "E322", {"start": v(-303.5, -5.5) * mm, "end": v(-312.7, -5.5) * mm});
            skLineSegment(sketch, "E323", {"start": v(-312.7, -5.5) * mm, "end": v(-312.7, -13.25) * mm});
            skLineSegment(sketch, "E324", {"start": v(-312.7, -13.25) * mm, "end": v(-301.77, -13.25) * mm});
            skLineSegment(sketch, "E325", {"start": v(-301.77, -13.25) * mm, "end": v(-301.77, -15.25) * mm});
            skLineSegment(sketch, "E326", {"start": v(-301.77, -15.25) * mm, "end": v(-314.7, -15.25) * mm});
            skLineSegment(sketch, "E327", {"start": v(-314.7, -15.25) * mm, "end": v(-314.7, 6) * mm});
            skLineSegment(sketch, "E328", {"start": v(-276.6, 47.5) * mm, "end": v(-263.66, 47.5) * mm});
            skLineSegment(sketch, "E329", {"start": v(-263.66, 47.5) * mm, "end": v(-263.66, 45.5) * mm});
            skLineSegment(sketch, "E330", {"start": v(-263.66, 45.5) * mm, "end": v(-274.6, 45.5) * mm});
            skLineSegment(sketch, "E331", {"start": v(-274.6, 45.5) * mm, "end": v(-274.6, 38) * mm});
            skLineSegment(sketch, "E332", {"start": v(-274.6, 38) * mm, "end": v(-265.38, 38) * mm});
            skLineSegment(sketch, "E333", {"start": v(-265.38, 38) * mm, "end": v(-265.38, 36) * mm});
            skLineSegment(sketch, "E334", {"start": v(-265.38, 36) * mm, "end": v(-274.6, 36) * mm});
            skLineSegment(sketch, "E335", {"start": v(-274.6, 36) * mm, "end": v(-274.6, 28.25) * mm});
            skLineSegment(sketch, "E336", {"start": v(-274.6, 28.25) * mm, "end": v(-263.66, 28.25) * mm});
            skLineSegment(sketch, "E337", {"start": v(-263.66, 28.25) * mm, "end": v(-263.66, 26.25) * mm});
            skLineSegment(sketch, "E338", {"start": v(-263.66, 26.25) * mm, "end": v(-276.6, 26.25) * mm});
            skLineSegment(sketch, "E339", {"start": v(-276.6, 26.25) * mm, "end": v(-276.6, 47.5) * mm});
            skLineSegment(sketch, "E340", {"start": v(-276.17, -35.5) * mm, "end": v(-263.23, -35.5) * mm});
            skLineSegment(sketch, "E341", {"start": v(-263.23, -35.5) * mm, "end": v(-263.23, -37.5) * mm});
            skLineSegment(sketch, "E342", {"start": v(-263.23, -37.5) * mm, "end": v(-274.17, -37.5) * mm});
            skLineSegment(sketch, "E343", {"start": v(-274.17, -37.5) * mm, "end": v(-274.17, -45) * mm});
            skLineSegment(sketch, "E344", {"start": v(-274.17, -45) * mm, "end": v(-264.95, -45) * mm});
            skLineSegment(sketch, "E345", {"start": v(-264.95, -45) * mm, "end": v(-264.95, -47) * mm});
            skLineSegment(sketch, "E346", {"start": v(-264.95, -47) * mm, "end": v(-274.17, -47) * mm});
            skLineSegment(sketch, "E347", {"start": v(-274.17, -47) * mm, "end": v(-274.17, -54.75) * mm});
            skLineSegment(sketch, "E348", {"start": v(-274.17, -54.75) * mm, "end": v(-263.23, -54.75) * mm});
            skLineSegment(sketch, "E349", {"start": v(-263.23, -54.75) * mm, "end": v(-263.23, -56.75) * mm});
            skLineSegment(sketch, "E350", {"start": v(-263.23, -56.75) * mm, "end": v(-276.17, -56.75) * mm});
            skLineSegment(sketch, "E351", {"start": v(-276.17, -56.75) * mm, "end": v(-276.17, -35.5) * mm});
            skLineSegment(sketch, "E352", {"start": v(-201.22, -35.5) * mm, "end": v(-188.28, -35.5) * mm});
            skLineSegment(sketch, "E353", {"start": v(-188.28, -35.5) * mm, "end": v(-188.28, -37.5) * mm});
            skLineSegment(sketch, "E354", {"start": v(-188.28, -37.5) * mm, "end": v(-199.22, -37.5) * mm});
            skLineSegment(sketch, "E355", {"start": v(-199.22, -37.5) * mm, "end": v(-199.22, -45) * mm});
            skLineSegment(sketch, "E356", {"start": v(-199.22, -45) * mm, "end": v(-190, -45) * mm});
            skLineSegment(sketch, "E357", {"start": v(-190, -45) * mm, "end": v(-190, -47) * mm});
            skLineSegment(sketch, "E358", {"start": v(-190, -47) * mm, "end": v(-199.22, -47) * mm});
            skLineSegment(sketch, "E359", {"start": v(-199.22, -47) * mm, "end": v(-199.22, -54.75) * mm});
            skLineSegment(sketch, "E360", {"start": v(-199.22, -54.75) * mm, "end": v(-188.28, -54.75) * mm});
            skLineSegment(sketch, "E361", {"start": v(-188.28, -54.75) * mm, "end": v(-188.28, -56.75) * mm});
            skLineSegment(sketch, "E362", {"start": v(-188.28, -56.75) * mm, "end": v(-201.22, -56.75) * mm});
            skLineSegment(sketch, "E363", {"start": v(-201.22, -56.75) * mm, "end": v(-201.22, -35.5) * mm});
            skLineSegment(sketch, "E364", {"start": v(-313.86, -76.14) * mm, "end": v(-300.92, -76.14) * mm});
            skLineSegment(sketch, "E365", {"start": v(-300.92, -76.14) * mm, "end": v(-300.92, -78.14) * mm});
            skLineSegment(sketch, "E366", {"start": v(-300.92, -78.14) * mm, "end": v(-311.86, -78.14) * mm});
            skLineSegment(sketch, "E367", {"start": v(-311.86, -78.14) * mm, "end": v(-311.86, -85.66) * mm});
            skLineSegment(sketch, "E368", {"start": v(-311.86, -85.66) * mm, "end": v(-302.64, -85.66) * mm});
            skLineSegment(sketch, "E369", {"start": v(-302.64, -85.66) * mm, "end": v(-302.64, -87.66) * mm});
            skLineSegment(sketch, "E370", {"start": v(-302.64, -87.66) * mm, "end": v(-311.86, -87.66) * mm});
            skLineSegment(sketch, "E371", {"start": v(-311.86, -87.66) * mm, "end": v(-311.86, -95.4) * mm});
            skLineSegment(sketch, "E372", {"start": v(-311.86, -95.4) * mm, "end": v(-300.92, -95.4) * mm});
            skLineSegment(sketch, "E373", {"start": v(-300.92, -95.4) * mm, "end": v(-300.92, -97.4) * mm});
            skLineSegment(sketch, "E374", {"start": v(-300.92, -97.4) * mm, "end": v(-313.86, -97.4) * mm});
            skLineSegment(sketch, "E375", {"start": v(-313.86, -97.4) * mm, "end": v(-313.86, -76.14) * mm});
            skLineSegment(sketch, "E376", {"start": v(-201.22, -77) * mm, "end": v(-188.28, -77) * mm});
            skLineSegment(sketch, "E377", {"start": v(-188.28, -77) * mm, "end": v(-188.28, -79) * mm});
            skLineSegment(sketch, "E378", {"start": v(-188.28, -79) * mm, "end": v(-199.22, -79) * mm});
            skLineSegment(sketch, "E379", {"start": v(-199.22, -79) * mm, "end": v(-199.22, -86.5) * mm});
            skLineSegment(sketch, "E380", {"start": v(-199.22, -86.5) * mm, "end": v(-190, -86.5) * mm});
            skLineSegment(sketch, "E381", {"start": v(-190, -86.5) * mm, "end": v(-190, -88.5) * mm});
            skLineSegment(sketch, "E382", {"start": v(-190, -88.5) * mm, "end": v(-199.22, -88.5) * mm});
            skLineSegment(sketch, "E383", {"start": v(-199.22, -88.5) * mm, "end": v(-199.22, -96.25) * mm});
            skLineSegment(sketch, "E384", {"start": v(-199.22, -96.25) * mm, "end": v(-188.28, -96.25) * mm});
            skLineSegment(sketch, "E385", {"start": v(-188.28, -96.25) * mm, "end": v(-188.28, -98.25) * mm});
            skLineSegment(sketch, "E386", {"start": v(-188.28, -98.25) * mm, "end": v(-201.22, -98.25) * mm});
            skLineSegment(sketch, "E387", {"start": v(-201.22, -98.25) * mm, "end": v(-201.22, -77) * mm});
            skLineSegment(sketch, "E388", {"start": v(-126.22, 212.86) * mm, "end": v(-113.28, 212.86) * mm});
            skLineSegment(sketch, "E389", {"start": v(-113.28, 212.86) * mm, "end": v(-113.28, 210.86) * mm});
            skLineSegment(sketch, "E390", {"start": v(-113.28, 210.86) * mm, "end": v(-124.22, 210.86) * mm});
            skLineSegment(sketch, "E391", {"start": v(-124.22, 210.86) * mm, "end": v(-124.22, 203.34) * mm});
            skLineSegment(sketch, "E392", {"start": v(-124.22, 203.34) * mm, "end": v(-115, 203.34) * mm});
            skLineSegment(sketch, "E393", {"start": v(-115, 203.34) * mm, "end": v(-115, 201.34) * mm});
            skLineSegment(sketch, "E394", {"start": v(-115, 201.34) * mm, "end": v(-124.22, 201.34) * mm});
            skLineSegment(sketch, "E395", {"start": v(-124.22, 201.34) * mm, "end": v(-124.22, 193.6) * mm});
            skLineSegment(sketch, "E396", {"start": v(-124.22, 193.6) * mm, "end": v(-113.28, 193.6) * mm});
            skLineSegment(sketch, "E397", {"start": v(-113.28, 193.6) * mm, "end": v(-113.28, 191.6) * mm});
            skLineSegment(sketch, "E398", {"start": v(-113.28, 191.6) * mm, "end": v(-126.22, 191.6) * mm});
            skLineSegment(sketch, "E399", {"start": v(-126.22, 191.6) * mm, "end": v(-126.22, 212.86) * mm});
            skLineSegment(sketch, "E400", {"start": v(-12.92, 213.4) * mm, "end": v(0.02, 213.4) * mm});
            skLineSegment(sketch, "E401", {"start": v(0.02, 213.4) * mm, "end": v(0.02, 211.4) * mm});
            skLineSegment(sketch, "E402", {"start": v(0.02, 211.4) * mm, "end": v(-10.92, 211.4) * mm});
            skLineSegment(sketch, "E403", {"start": v(-10.92, 211.4) * mm, "end": v(-10.92, 203.9) * mm});
            skLineSegment(sketch, "E404", {"start": v(-10.92, 203.9) * mm, "end": v(-1.7, 203.9) * mm});
            skLineSegment(sketch, "E405", {"start": v(-1.7, 203.9) * mm, "end": v(-1.7, 201.9) * mm});
            skLineSegment(sketch, "E406", {"start": v(-1.7, 201.9) * mm, "end": v(-10.92, 201.9) * mm});
            skLineSegment(sketch, "E407", {"start": v(-10.92, 201.9) * mm, "end": v(-10.92, 194.15) * mm});
            skLineSegment(sketch, "E408", {"start": v(-10.92, 194.15) * mm, "end": v(0.02, 194.15) * mm});
            skLineSegment(sketch, "E409", {"start": v(0.02, 194.15) * mm, "end": v(0.02, 192.15) * mm});
            skLineSegment(sketch, "E410", {"start": v(0.02, 192.15) * mm, "end": v(-12.92, 192.15) * mm});
            skLineSegment(sketch, "E411", {"start": v(-12.92, 192.15) * mm, "end": v(-12.92, 213.4) * mm});
            skLineSegment(sketch, "E412", {"start": v(-12.92, 89.26) * mm, "end": v(0.02, 89.26) * mm});
            skLineSegment(sketch, "E413", {"start": v(0.02, 89.26) * mm, "end": v(0.02, 87.26) * mm});
            skLineSegment(sketch, "E414", {"start": v(0.02, 87.26) * mm, "end": v(-10.92, 87.26) * mm});
            skLineSegment(sketch, "E415", {"start": v(-10.92, 87.26) * mm, "end": v(-10.92, 79.75) * mm});
            skLineSegment(sketch, "E416", {"start": v(-10.92, 79.75) * mm, "end": v(-1.7, 79.75) * mm});
            skLineSegment(sketch, "E417", {"start": v(-1.7, 79.75) * mm, "end": v(-1.7, 77.75) * mm});
            skLineSegment(sketch, "E418", {"start": v(-1.7, 77.75) * mm, "end": v(-10.92, 77.75) * mm});
            skLineSegment(sketch, "E419", {"start": v(-10.92, 77.75) * mm, "end": v(-10.92, 70) * mm});
            skLineSegment(sketch, "E420", {"start": v(-10.92, 70) * mm, "end": v(0.02, 70) * mm});
            skLineSegment(sketch, "E421", {"start": v(0.02, 70) * mm, "end": v(0.02, 68) * mm});
            skLineSegment(sketch, "E422", {"start": v(0.02, 68) * mm, "end": v(-12.92, 68) * mm});
            skLineSegment(sketch, "E423", {"start": v(-12.92, 68) * mm, "end": v(-12.92, 89.26) * mm});
            skLineSegment(sketch, "E424", {"start": v(-276.58, 213.15) * mm, "end": v(-263.64, 213.15) * mm});
            skLineSegment(sketch, "E425", {"start": v(-263.64, 213.15) * mm, "end": v(-263.64, 211.15) * mm});
            skLineSegment(sketch, "E426", {"start": v(-263.64, 211.15) * mm, "end": v(-274.58, 211.15) * mm});
            skLineSegment(sketch, "E427", {"start": v(-274.58, 211.15) * mm, "end": v(-274.58, 203.63) * mm});
            skLineSegment(sketch, "E428", {"start": v(-274.58, 203.63) * mm, "end": v(-265.36, 203.63) * mm});
            skLineSegment(sketch, "E429", {"start": v(-265.36, 203.63) * mm, "end": v(-265.36, 201.63) * mm});
            skLineSegment(sketch, "E430", {"start": v(-265.36, 201.63) * mm, "end": v(-274.58, 201.63) * mm});
            skLineSegment(sketch, "E431", {"start": v(-274.58, 201.63) * mm, "end": v(-274.58, 193.89) * mm});
            skLineSegment(sketch, "E432", {"start": v(-274.58, 193.89) * mm, "end": v(-263.64, 193.89) * mm});
            skLineSegment(sketch, "E433", {"start": v(-263.64, 193.89) * mm, "end": v(-263.64, 191.89) * mm});
            skLineSegment(sketch, "E434", {"start": v(-263.64, 191.89) * mm, "end": v(-276.58, 191.89) * mm});
            skLineSegment(sketch, "E435", {"start": v(-276.58, 191.89) * mm, "end": v(-276.58, 213.15) * mm});
            skLineSegment(sketch, "E436", {"start": v(-352.53, 297.34) * mm, "end": v(-339.6, 297.34) * mm});
            skLineSegment(sketch, "E437", {"start": v(-339.6, 297.34) * mm, "end": v(-339.6, 295.34) * mm});
            skLineSegment(sketch, "E438", {"start": v(-339.6, 295.34) * mm, "end": v(-350.53, 295.34) * mm});
            skLineSegment(sketch, "E439", {"start": v(-350.53, 295.34) * mm, "end": v(-350.53, 287.58) * mm});
            skLineSegment(sketch, "E440", {"start": v(-350.53, 287.58) * mm, "end": v(-341.3, 287.58) * mm});
            skLineSegment(sketch, "E441", {"start": v(-341.3, 287.58) * mm, "end": v(-341.3, 285.58) * mm});
            skLineSegment(sketch, "E442", {"start": v(-341.3, 285.58) * mm, "end": v(-350.53, 285.58) * mm});
            skLineSegment(sketch, "E443", {"start": v(-350.53, 285.58) * mm, "end": v(-350.53, 277.84) * mm});
            skLineSegment(sketch, "E444", {"start": v(-350.53, 277.84) * mm, "end": v(-339.6, 277.84) * mm});
            skLineSegment(sketch, "E445", {"start": v(-339.6, 277.84) * mm, "end": v(-339.6, 275.84) * mm});
            skLineSegment(sketch, "E446", {"start": v(-339.6, 275.84) * mm, "end": v(-352.53, 275.84) * mm});
            skLineSegment(sketch, "E447", {"start": v(-352.53, 275.84) * mm, "end": v(-352.53, 297.34) * mm});
            skLineSegment(sketch, "E448", {"start": v(-12.76, 48.2) * mm, "end": v(0.18, 48.2) * mm});
            skLineSegment(sketch, "E449", {"start": v(0.18, 48.2) * mm, "end": v(0.18, 46.2) * mm});
            skLineSegment(sketch, "E450", {"start": v(0.18, 46.2) * mm, "end": v(-10.76, 46.2) * mm});
            skLineSegment(sketch, "E451", {"start": v(-10.76, 46.2) * mm, "end": v(-10.76, 38.68) * mm});
            skLineSegment(sketch, "E452", {"start": v(-10.76, 38.68) * mm, "end": v(-1.54, 38.68) * mm});
            skLineSegment(sketch, "E453", {"start": v(-1.54, 38.68) * mm, "end": v(-1.54, 36.68) * mm});
            skLineSegment(sketch, "E454", {"start": v(-1.54, 36.68) * mm, "end": v(-10.76, 36.68) * mm});
            skLineSegment(sketch, "E455", {"start": v(-10.76, 36.68) * mm, "end": v(-10.76, 28.94) * mm});
            skLineSegment(sketch, "E456", {"start": v(-10.76, 28.94) * mm, "end": v(0.18, 28.94) * mm});
            skLineSegment(sketch, "E457", {"start": v(0.18, 28.94) * mm, "end": v(0.18, 26.94) * mm});
            skLineSegment(sketch, "E458", {"start": v(0.18, 26.94) * mm, "end": v(-12.76, 26.94) * mm});
            skLineSegment(sketch, "E459", {"start": v(-12.76, 26.94) * mm, "end": v(-12.76, 48.2) * mm});
            skLineSegment(sketch, "E460", {"start": v(-310.48, 285.87) * mm, "end": v(-306.92, 285.2) * mm});
            skArc(sketch, "E461", {"start": v(-306.92, 285.2) * mm, "mid": v(-303.91, 281.2) * mm, "end": v(-307.6, 277.84) * mm});
            skLineSegment(sketch, "E462", {"start": v(-310.87, 287.98) * mm, "end": v(-306.45, 287.14) * mm});
            skArc(sketch, "E463", {"start": v(-306.45, 287.14) * mm, "mid": v(-301.84, 281) * mm, "end": v(-307.51, 275.84) * mm});
            skLineSegment(sketch, "E464", {"start": v(-307.6, 277.84) * mm, "end": v(-309.65, 277.84) * mm});
            skLineSegment(sketch, "E465", {"start": v(-307.51, 275.84) * mm, "end": v(-309.65, 275.84) * mm});
            skArc(sketch, "E466", {"start": v(-309.65, 277.84) * mm, "mid": v(-312.43, 278.46) * mm, "end": v(-314.68, 280.22) * mm});
            skArc(sketch, "E467", {"start": v(-309.65, 275.84) * mm, "mid": v(-313.22, 276.62) * mm, "end": v(-316.12, 278.83) * mm});
            skLineSegment(sketch, "E468", {"start": v(-316.12, 278.83) * mm, "end": v(-314.68, 280.22) * mm});
            skLineSegment(sketch, "E469", {"start": v(-304.03, 293.22) * mm, "end": v(-302.54, 294.55) * mm});
            skLineSegment(sketch, "E470", {"start": v(-309.78, 297.34) * mm, "end": v(-308.35, 297.34) * mm});
            skLineSegment(sketch, "E471", {"start": v(-309.71, 295.34) * mm, "end": v(-308.41, 295.34) * mm});
            skArc(sketch, "E472", {"start": v(-308.35, 297.34) * mm, "mid": v(-305.13, 296.6) * mm, "end": v(-302.54, 294.55) * mm});
            skArc(sketch, "E473", {"start": v(-308.41, 295.34) * mm, "mid": v(-305.98, 294.78) * mm, "end": v(-304.03, 293.22) * mm});
            skArc(sketch, "E474", {"start": v(-309.71, 295.34) * mm, "mid": v(-313.44, 292.15) * mm, "end": v(-310.87, 287.98) * mm});
            skArc(sketch, "E475", {"start": v(-309.78, 297.34) * mm, "mid": v(-315.52, 291.93) * mm, "end": v(-310.48, 285.87) * mm});
            skLineSegment(sketch, "E476", {"start": v(-197.4, 285.87) * mm, "end": v(-193.84, 285.2) * mm});
            skArc(sketch, "E477", {"start": v(-193.84, 285.2) * mm, "mid": v(-190.83, 281.2) * mm, "end": v(-194.53, 277.84) * mm});
            skLineSegment(sketch, "E478", {"start": v(-197.8, 287.98) * mm, "end": v(-193.37, 287.14) * mm});
            skArc(sketch, "E479", {"start": v(-193.37, 287.14) * mm, "mid": v(-188.76, 281) * mm, "end": v(-194.43, 275.84) * mm});
            skLineSegment(sketch, "E480", {"start": v(-194.53, 277.84) * mm, "end": v(-196.57, 277.84) * mm});
            skLineSegment(sketch, "E481", {"start": v(-194.43, 275.84) * mm, "end": v(-196.57, 275.84) * mm});
            skArc(sketch, "E482", {"start": v(-196.57, 277.84) * mm, "mid": v(-199.35, 278.46) * mm, "end": v(-201.6, 280.22) * mm});
            skArc(sketch, "E483", {"start": v(-196.57, 275.84) * mm, "mid": v(-200.13, 276.62) * mm, "end": v(-203.04, 278.83) * mm});
            skLineSegment(sketch, "E484", {"start": v(-203.04, 278.83) * mm, "end": v(-201.6, 280.22) * mm});
            skLineSegment(sketch, "E485", {"start": v(-190.95, 293.22) * mm, "end": v(-189.46, 294.55) * mm});
            skLineSegment(sketch, "E486", {"start": v(-196.7, 297.34) * mm, "end": v(-195.26, 297.34) * mm});
            skLineSegment(sketch, "E487", {"start": v(-196.63, 295.34) * mm, "end": v(-195.33, 295.34) * mm});
            skArc(sketch, "E488", {"start": v(-195.26, 297.34) * mm, "mid": v(-192.05, 296.6) * mm, "end": v(-189.46, 294.55) * mm});
            skArc(sketch, "E489", {"start": v(-195.33, 295.34) * mm, "mid": v(-192.9, 294.78) * mm, "end": v(-190.95, 293.22) * mm});
            skArc(sketch, "E490", {"start": v(-196.63, 295.34) * mm, "mid": v(-200.36, 292.15) * mm, "end": v(-197.8, 287.98) * mm});
            skArc(sketch, "E491", {"start": v(-196.7, 297.34) * mm, "mid": v(-202.44, 291.93) * mm, "end": v(-197.4, 285.87) * mm});
            skLineSegment(sketch, "E492", {"start": v(-348.67, -4.75) * mm, "end": v(-345.07, -5.43) * mm});
            skArc(sketch, "E493", {"start": v(-345.07, -5.43) * mm, "mid": v(-342.1, -9.32) * mm, "end": v(-345.66, -12.69) * mm});
            skLineSegment(sketch, "E494", {"start": v(-349.06, -2.64) * mm, "end": v(-344.6, -3.49) * mm});
            skArc(sketch, "E495", {"start": v(-344.6, -3.49) * mm, "mid": v(-340.03, -9.5) * mm, "end": v(-345.51, -14.68) * mm});
            skLineSegment(sketch, "E496", {"start": v(-345.66, -12.69) * mm, "end": v(-347.63, -12.74) * mm});
            skLineSegment(sketch, "E497", {"start": v(-345.51, -14.68) * mm, "end": v(-347.63, -14.74) * mm});
            skArc(sketch, "E498", {"start": v(-347.63, -12.74) * mm, "mid": v(-350.52, -12.15) * mm, "end": v(-352.87, -10.36) * mm});
            skArc(sketch, "E499", {"start": v(-347.63, -14.74) * mm, "mid": v(-351.3, -14) * mm, "end": v(-354.31, -11.75) * mm});
            skLineSegment(sketch, "E500", {"start": v(-354.31, -11.75) * mm, "end": v(-352.87, -10.36) * mm});
            skLineSegment(sketch, "E501", {"start": v(-342.23, 2.6) * mm, "end": v(-340.73, 3.93) * mm});
            skLineSegment(sketch, "E502", {"start": v(-347.97, 6.71) * mm, "end": v(-346.54, 6.71) * mm});
            skLineSegment(sketch, "E503", {"start": v(-347.9, 4.71) * mm, "end": v(-346.6, 4.71) * mm});
            skArc(sketch, "E504", {"start": v(-346.54, 6.71) * mm, "mid": v(-343.32, 5.98) * mm, "end": v(-340.73, 3.93) * mm});
            skArc(sketch, "E505", {"start": v(-346.6, 4.71) * mm, "mid": v(-344.17, 4.16) * mm, "end": v(-342.23, 2.6) * mm});
            skArc(sketch, "E506", {"start": v(-347.9, 4.71) * mm, "mid": v(-351.63, 1.53) * mm, "end": v(-349.06, -2.64) * mm});
            skArc(sketch, "E507", {"start": v(-347.97, 6.71) * mm, "mid": v(-353.72, 1.3) * mm, "end": v(-348.67, -4.75) * mm});
            skLineSegment(sketch, "E508", {"start": v(-348.52, -46.08) * mm, "end": v(-344.92, -46.76) * mm});
            skArc(sketch, "E509", {"start": v(-344.92, -46.76) * mm, "mid": v(-341.96, -50.65) * mm, "end": v(-345.5, -54.01) * mm});
            skLineSegment(sketch, "E510", {"start": v(-348.92, -43.97) * mm, "end": v(-344.46, -44.81) * mm});
            skArc(sketch, "E511", {"start": v(-344.46, -44.81) * mm, "mid": v(-339.88, -50.82) * mm, "end": v(-345.36, -56.01) * mm});
            skLineSegment(sketch, "E512", {"start": v(-345.5, -54.01) * mm, "end": v(-347.48, -54.06) * mm});
            skLineSegment(sketch, "E513", {"start": v(-345.36, -56.01) * mm, "end": v(-347.48, -56.06) * mm});
            skArc(sketch, "E514", {"start": v(-347.48, -54.06) * mm, "mid": v(-350.38, -53.48) * mm, "end": v(-352.72, -51.69) * mm});
            skArc(sketch, "E515", {"start": v(-347.48, -56.06) * mm, "mid": v(-351.16, -55.33) * mm, "end": v(-354.16, -53.07) * mm});
            skLineSegment(sketch, "E516", {"start": v(-354.16, -53.07) * mm, "end": v(-352.72, -51.69) * mm});
            skLineSegment(sketch, "E517", {"start": v(-342.08, -38.73) * mm, "end": v(-340.59, -37.4) * mm});
            skLineSegment(sketch, "E518", {"start": v(-347.83, -34.61) * mm, "end": v(-346.4, -34.61) * mm});
            skLineSegment(sketch, "E519", {"start": v(-347.76, -36.61) * mm, "end": v(-346.46, -36.61) * mm});
            skArc(sketch, "E520", {"start": v(-346.4, -34.61) * mm, "mid": v(-343.17, -35.35) * mm, "end": v(-340.59, -37.4) * mm});
            skArc(sketch, "E521", {"start": v(-346.46, -36.61) * mm, "mid": v(-344.02, -37.17) * mm, "end": v(-342.08, -38.73) * mm});
            skArc(sketch, "E522", {"start": v(-347.76, -36.61) * mm, "mid": v(-351.48, -39.8) * mm, "end": v(-348.92, -43.97) * mm});
            skArc(sketch, "E523", {"start": v(-347.83, -34.61) * mm, "mid": v(-353.57, -40.02) * mm, "end": v(-348.52, -46.08) * mm});
            skLineSegment(sketch, "E524", {"start": v(-197.51, -4.84) * mm, "end": v(-193.92, -5.52) * mm});
            skArc(sketch, "E525", {"start": v(-193.92, -5.52) * mm, "mid": v(-190.95, -9.41) * mm, "end": v(-194.5, -12.77) * mm});
            skLineSegment(sketch, "E526", {"start": v(-197.91, -2.73) * mm, "end": v(-193.45, -3.58) * mm});
            skArc(sketch, "E527", {"start": v(-193.45, -3.58) * mm, "mid": v(-188.87, -9.58) * mm, "end": v(-194.36, -14.77) * mm});
            skLineSegment(sketch, "E528", {"start": v(-194.5, -12.77) * mm, "end": v(-196.47, -12.82) * mm});
            skLineSegment(sketch, "E529", {"start": v(-194.36, -14.77) * mm, "end": v(-196.47, -14.83) * mm});
            skArc(sketch, "E530", {"start": v(-196.47, -12.82) * mm, "mid": v(-199.37, -12.24) * mm, "end": v(-201.72, -10.45) * mm});
            skArc(sketch, "E531", {"start": v(-196.47, -14.83) * mm, "mid": v(-200.15, -14.09) * mm, "end": v(-203.16, -11.83) * mm});
            skLineSegment(sketch, "E532", {"start": v(-203.16, -11.83) * mm, "end": v(-201.72, -10.45) * mm});
            skLineSegment(sketch, "E533", {"start": v(-191.07, 2.5) * mm, "end": v(-189.58, 3.84) * mm});
            skLineSegment(sketch, "E534", {"start": v(-196.82, 6.63) * mm, "end": v(-195.38, 6.63) * mm});
            skLineSegment(sketch, "E535", {"start": v(-196.75, 4.63) * mm, "end": v(-195.45, 4.63) * mm});
            skArc(sketch, "E536", {"start": v(-195.38, 6.63) * mm, "mid": v(-192.17, 5.9) * mm, "end": v(-189.58, 3.84) * mm});
            skArc(sketch, "E537", {"start": v(-195.45, 4.63) * mm, "mid": v(-193.02, 4.07) * mm, "end": v(-191.07, 2.5) * mm});
            skArc(sketch, "E538", {"start": v(-196.75, 4.63) * mm, "mid": v(-200.48, 1.44) * mm, "end": v(-197.91, -2.73) * mm});
            skArc(sketch, "E539", {"start": v(-196.82, 6.63) * mm, "mid": v(-202.56, 1.22) * mm, "end": v(-197.51, -4.84) * mm});
            skLineSegment(sketch, "E540", {"start": v(-276.97, 275.84) * mm, "end": v(-277.24, 297.34) * mm});
            skLineSegment(sketch, "E541", {"start": v(-277.24, 297.34) * mm, "end": v(-275.24, 297.34) * mm});
            skLineSegment(sketch, "E542", {"start": v(-275.24, 297.34) * mm, "end": v(-275.09, 285.52) * mm});
            skLineSegment(sketch, "E543", {"start": v(-275.09, 285.52) * mm, "end": v(-265.18, 297.34) * mm});
            skLineSegment(sketch, "E544", {"start": v(-265.18, 297.34) * mm, "end": v(-262.39, 297.55) * mm});
            skLineSegment(sketch, "E545", {"start": v(-262.39, 297.55) * mm, "end": v(-269.72, 288.82) * mm});
            skLineSegment(sketch, "E546", {"start": v(-269.72, 288.82) * mm, "end": v(-262.02, 275.84) * mm});
            skLineSegment(sketch, "E547", {"start": v(-262.02, 275.84) * mm, "end": v(-264.34, 275.84) * mm});
            skLineSegment(sketch, "E548", {"start": v(-264.34, 275.84) * mm, "end": v(-270.98, 287.03) * mm});
            skLineSegment(sketch, "E549", {"start": v(-270.98, 287.03) * mm, "end": v(-275.24, 281.97) * mm});
            skLineSegment(sketch, "E550", {"start": v(-275.24, 281.97) * mm, "end": v(-275.12, 275.84) * mm});
            skLineSegment(sketch, "E551", {"start": v(-275.12, 275.84) * mm, "end": v(-276.97, 275.84) * mm});
            skLineSegment(sketch, "E552", {"start": v(-88.28, -97.4) * mm, "end": v(-88.28, -75.82) * mm});
            skLineSegment(sketch, "E553", {"start": v(-88.28, -75.82) * mm, "end": v(-86.28, -75.82) * mm});
            skLineSegment(sketch, "E554", {"start": v(-86.28, -75.82) * mm, "end": v(-86.28, -87.91) * mm});
            skLineSegment(sketch, "E555", {"start": v(-86.28, -87.91) * mm, "end": v(-76.24, -75.82) * mm});
            skLineSegment(sketch, "E556", {"start": v(-76.24, -75.82) * mm, "end": v(-73.64, -75.82) * mm});
            skLineSegment(sketch, "E557", {"start": v(-73.64, -75.82) * mm, "end": v(-80.79, -84.42) * mm});
            skLineSegment(sketch, "E558", {"start": v(-80.79, -84.42) * mm, "end": v(-73.09, -97.4) * mm});
            skLineSegment(sketch, "E559", {"start": v(-73.09, -97.4) * mm, "end": v(-75.41, -97.4) * mm});
            skLineSegment(sketch, "E560", {"start": v(-75.41, -97.4) * mm, "end": v(-82.06, -86.2) * mm});
            skLineSegment(sketch, "E561", {"start": v(-82.06, -86.2) * mm, "end": v(-86.28, -91.3) * mm});
            skLineSegment(sketch, "E562", {"start": v(-86.28, -91.3) * mm, "end": v(-86.28, -97.4) * mm});
            skLineSegment(sketch, "E563", {"start": v(-86.28, -97.4) * mm, "end": v(-88.28, -97.4) * mm});
            skLineSegment(sketch, "E564", {"start": v(-234.2, 275.84) * mm, "end": v(-234.2, 297.34) * mm});
            skLineSegment(sketch, "E565", {"start": v(-234.2, 297.34) * mm, "end": v(-232.2, 297.34) * mm});
            skLineSegment(sketch, "E566", {"start": v(-232.2, 297.34) * mm, "end": v(-232.2, 275.84) * mm});
            skLineSegment(sketch, "E567", {"start": v(-232.2, 275.84) * mm, "end": v(-234.2, 275.84) * mm});
            skLineSegment(sketch, "E568", {"start": v(-234.35, 191.68) * mm, "end": v(-234.35, 212.98) * mm});
            skLineSegment(sketch, "E569", {"start": v(-234.35, 212.98) * mm, "end": v(-232.35, 212.98) * mm});
            skLineSegment(sketch, "E570", {"start": v(-232.35, 212.98) * mm, "end": v(-232.35, 191.68) * mm});
            skLineSegment(sketch, "E571", {"start": v(-232.35, 191.68) * mm, "end": v(-234.35, 191.68) * mm});
            skLineSegment(sketch, "E572", {"start": v(-158.78, 191.8) * mm, "end": v(-158.78, 213.11) * mm});
            skLineSegment(sketch, "E573", {"start": v(-158.78, 213.11) * mm, "end": v(-156.78, 213.11) * mm});
            skLineSegment(sketch, "E574", {"start": v(-156.78, 213.11) * mm, "end": v(-156.78, 191.8) * mm});
            skLineSegment(sketch, "E575", {"start": v(-156.78, 191.8) * mm, "end": v(-158.78, 191.8) * mm});
            skLineSegment(sketch, "E576", {"start": v(-7.87, 234.18) * mm, "end": v(-7.87, 255.68) * mm});
            skLineSegment(sketch, "E577", {"start": v(-7.87, 255.68) * mm, "end": v(-5.87, 255.68) * mm});
            skLineSegment(sketch, "E578", {"start": v(-5.87, 255.68) * mm, "end": v(-5.87, 234.18) * mm});
            skLineSegment(sketch, "E579", {"start": v(-5.87, 234.18) * mm, "end": v(-7.87, 234.18) * mm});
            skLineSegment(sketch, "E580", {"start": v(-45.54, 26.4) * mm, "end": v(-45.54, 47.7) * mm});
            skLineSegment(sketch, "E581", {"start": v(-45.54, 47.7) * mm, "end": v(-43.54, 47.7) * mm});
            skLineSegment(sketch, "E582", {"start": v(-43.54, 47.7) * mm, "end": v(-43.54, 26.4) * mm});
            skLineSegment(sketch, "E583", {"start": v(-43.54, 26.4) * mm, "end": v(-45.54, 26.4) * mm});
            skLineSegment(sketch, "E584", {"start": v(29.48, 67.92) * mm, "end": v(29.48, 89.22) * mm});
            skLineSegment(sketch, "E585", {"start": v(29.48, 89.22) * mm, "end": v(31.48, 89.22) * mm});
            skLineSegment(sketch, "E586", {"start": v(31.48, 89.22) * mm, "end": v(31.48, 67.92) * mm});
            skLineSegment(sketch, "E587", {"start": v(31.48, 67.92) * mm, "end": v(29.48, 67.92) * mm});
            skLineSegment(sketch, "E588", {"start": v(-234.43, 26.58) * mm, "end": v(-234.43, 47.88) * mm});
            skLineSegment(sketch, "E589", {"start": v(-234.43, 47.88) * mm, "end": v(-232.43, 47.88) * mm});
            skLineSegment(sketch, "E590", {"start": v(-232.43, 47.88) * mm, "end": v(-232.43, 26.58) * mm});
            skLineSegment(sketch, "E591", {"start": v(-232.43, 26.58) * mm, "end": v(-234.43, 26.58) * mm});
            skLineSegment(sketch, "E592", {"start": v(-309.83, -56.49) * mm, "end": v(-309.83, -35.19) * mm});
            skLineSegment(sketch, "E593", {"start": v(-309.83, -35.19) * mm, "end": v(-307.83, -35.19) * mm});
            skLineSegment(sketch, "E594", {"start": v(-307.83, -35.19) * mm, "end": v(-307.83, -56.49) * mm});
            skLineSegment(sketch, "E595", {"start": v(-307.83, -56.49) * mm, "end": v(-309.83, -56.49) * mm});
            skLineSegment(sketch, "E596", {"start": v(-158.99, 275.84) * mm, "end": v(-156.99, 275.84) * mm});
            skLineSegment(sketch, "E597", {"start": v(-156.99, 275.84) * mm, "end": v(-156.99, 295.34) * mm});
            skLineSegment(sketch, "E598", {"start": v(-156.99, 295.34) * mm, "end": v(-150.67, 295.34) * mm});
            skLineSegment(sketch, "E599", {"start": v(-150.67, 295.34) * mm, "end": v(-150.67, 297.34) * mm});
            skLineSegment(sketch, "E600", {"start": v(-150.67, 297.34) * mm, "end": v(-164.73, 297.34) * mm});
            skLineSegment(sketch, "E601", {"start": v(-164.73, 297.34) * mm, "end": v(-164.73, 295.34) * mm});
            skLineSegment(sketch, "E602", {"start": v(-164.73, 295.34) * mm, "end": v(-158.99, 295.34) * mm});
            skLineSegment(sketch, "E603", {"start": v(-158.99, 295.34) * mm, "end": v(-158.99, 275.84) * mm});
            skLineSegment(sketch, "E604", {"start": v(-45.62, 192.15) * mm, "end": v(-43.62, 192.15) * mm});
            skLineSegment(sketch, "E605", {"start": v(-43.62, 192.15) * mm, "end": v(-43.62, 211) * mm});
            skLineSegment(sketch, "E606", {"start": v(-43.62, 211) * mm, "end": v(-37.6, 211) * mm});
            skLineSegment(sketch, "E607", {"start": v(-37.6, 211) * mm, "end": v(-37.6, 213) * mm});
            skLineSegment(sketch, "E608", {"start": v(-37.6, 213) * mm, "end": v(-51.66, 213) * mm});
            skLineSegment(sketch, "E609", {"start": v(-51.66, 213) * mm, "end": v(-51.66, 211) * mm});
            skLineSegment(sketch, "E610", {"start": v(-51.66, 211) * mm, "end": v(-45.62, 211) * mm});
            skLineSegment(sketch, "E611", {"start": v(-45.62, 211) * mm, "end": v(-45.62, 192.15) * mm});
            skLineSegment(sketch, "E612", {"start": v(-129.2, 275.9) * mm, "end": v(-120.8, 297.27) * mm});
            skLineSegment(sketch, "E613", {"start": v(-120.8, 297.27) * mm, "end": v(-119.85, 297.26) * mm});
            skLineSegment(sketch, "E614", {"start": v(-119.85, 297.26) * mm, "end": v(-111.7, 275.9) * mm});
            skLineSegment(sketch, "E615", {"start": v(-111.7, 275.9) * mm, "end": v(-113.95, 275.9) * mm});
            skLineSegment(sketch, "E616", {"start": v(-113.95, 275.9) * mm, "end": v(-115.62, 280.28) * mm});
            skLineSegment(sketch, "E617", {"start": v(-115.62, 280.28) * mm, "end": v(-121.02, 280.28) * mm});
            skLineSegment(sketch, "E618", {"start": v(-121.02, 280.28) * mm, "end": v(-121.02, 282.28) * mm});
            skLineSegment(sketch, "E619", {"start": v(-121.02, 282.28) * mm, "end": v(-116.28, 282.28) * mm});
            skLineSegment(sketch, "E620", {"start": v(-116.28, 282.28) * mm, "end": v(-120.34, 292.94) * mm});
            skLineSegment(sketch, "E621", {"start": v(-120.34, 292.94) * mm, "end": v(-127.06, 275.86) * mm});
            skLineSegment(sketch, "E622", {"start": v(-127.06, 275.86) * mm, "end": v(-129.2, 275.9) * mm});
            skLineSegment(sketch, "E623", {"start": v(-128.12, 234.1) * mm, "end": v(-119.66, 255.6) * mm});
            skLineSegment(sketch, "E624", {"start": v(-119.66, 255.6) * mm, "end": v(-118.82, 255.6) * mm});
            skLineSegment(sketch, "E625", {"start": v(-118.82, 255.6) * mm, "end": v(-110.63, 234.1) * mm});
            skLineSegment(sketch, "E626", {"start": v(-110.63, 234.1) * mm, "end": v(-112.87, 234.1) * mm});
            skLineSegment(sketch, "E627", {"start": v(-112.87, 234.1) * mm, "end": v(-114.9, 239.4) * mm});
            skLineSegment(sketch, "E628", {"start": v(-114.9, 239.4) * mm, "end": v(-119.94, 239.4) * mm});
            skLineSegment(sketch, "E629", {"start": v(-119.94, 239.4) * mm, "end": v(-119.94, 241.4) * mm});
            skLineSegment(sketch, "E630", {"start": v(-119.94, 241.4) * mm, "end": v(-115.55, 241.4) * mm});
            skLineSegment(sketch, "E631", {"start": v(-115.55, 241.4) * mm, "end": v(-119.26, 251.14) * mm});
            skLineSegment(sketch, "E632", {"start": v(-119.26, 251.14) * mm, "end": v(-125.97, 234.1) * mm});
            skLineSegment(sketch, "E633", {"start": v(-125.97, 234.1) * mm, "end": v(-128.12, 234.1) * mm});
            skLineSegment(sketch, "E634", {"start": v(-53.6, 152.22) * mm, "end": v(-45.2, 173.6) * mm});
            skLineSegment(sketch, "E635", {"start": v(-45.2, 173.6) * mm, "end": v(-44.26, 173.6) * mm});
            skLineSegment(sketch, "E636", {"start": v(-44.26, 173.6) * mm, "end": v(-36.1, 152.22) * mm});
            skLineSegment(sketch, "E637", {"start": v(-36.1, 152.22) * mm, "end": v(-38.35, 152.22) * mm});
            skLineSegment(sketch, "E638", {"start": v(-38.35, 152.22) * mm, "end": v(-40.38, 157.53) * mm});
            skLineSegment(sketch, "E639", {"start": v(-40.38, 157.53) * mm, "end": v(-45.42, 157.53) * mm});
            skLineSegment(sketch, "E640", {"start": v(-45.42, 157.53) * mm, "end": v(-45.42, 159.53) * mm});
            skLineSegment(sketch, "E641", {"start": v(-45.42, 159.53) * mm, "end": v(-41.03, 159.53) * mm});
            skLineSegment(sketch, "E642", {"start": v(-41.03, 159.53) * mm, "end": v(-44.75, 169.27) * mm});
            skLineSegment(sketch, "E643", {"start": v(-44.75, 169.27) * mm, "end": v(-51.45, 152.22) * mm});
            skLineSegment(sketch, "E644", {"start": v(-51.45, 152.22) * mm, "end": v(-53.6, 152.22) * mm});
            skLineSegment(sketch, "E645", {"start": v(-204.54, 109.8) * mm, "end": v(-196.13, 131.18) * mm});
            skLineSegment(sketch, "E646", {"start": v(-196.13, 131.18) * mm, "end": v(-195.2, 131.18) * mm});
            skLineSegment(sketch, "E647", {"start": v(-195.2, 131.18) * mm, "end": v(-187.04, 109.8) * mm});
            skLineSegment(sketch, "E648", {"start": v(-187.04, 109.8) * mm, "end": v(-189.29, 109.8) * mm});
            skLineSegment(sketch, "E649", {"start": v(-189.29, 109.8) * mm, "end": v(-191.31, 115.11) * mm});
            skLineSegment(sketch, "E650", {"start": v(-191.31, 115.11) * mm, "end": v(-196.35, 115.11) * mm});
            skLineSegment(sketch, "E651", {"start": v(-196.35, 115.11) * mm, "end": v(-196.35, 117.11) * mm});
            skLineSegment(sketch, "E652", {"start": v(-196.35, 117.11) * mm, "end": v(-191.97, 117.11) * mm});
            skLineSegment(sketch, "E653", {"start": v(-191.97, 117.11) * mm, "end": v(-195.68, 126.85) * mm});
            skLineSegment(sketch, "E654", {"start": v(-195.68, 126.85) * mm, "end": v(-202.39, 109.8) * mm});
            skLineSegment(sketch, "E655", {"start": v(-202.39, 109.8) * mm, "end": v(-204.54, 109.8) * mm});
            skLineSegment(sketch, "E656", {"start": v(-166.99, 68.4) * mm, "end": v(-158.58, 89.79) * mm});
            skLineSegment(sketch, "E657", {"start": v(-158.58, 89.79) * mm, "end": v(-157.64, 89.79) * mm});
            skLineSegment(sketch, "E658", {"start": v(-157.64, 89.79) * mm, "end": v(-149.5, 68.4) * mm});
            skLineSegment(sketch, "E659", {"start": v(-149.5, 68.4) * mm, "end": v(-151.74, 68.4) * mm});
            skLineSegment(sketch, "E660", {"start": v(-151.74, 68.4) * mm, "end": v(-153.76, 73.72) * mm});
            skLineSegment(sketch, "E661", {"start": v(-153.76, 73.72) * mm, "end": v(-158.8, 73.72) * mm});
            skLineSegment(sketch, "E662", {"start": v(-158.8, 73.72) * mm, "end": v(-158.8, 75.72) * mm});
            skLineSegment(sketch, "E663", {"start": v(-158.8, 75.72) * mm, "end": v(-154.42, 75.72) * mm});
            skLineSegment(sketch, "E664", {"start": v(-154.42, 75.72) * mm, "end": v(-158.13, 85.46) * mm});
            skLineSegment(sketch, "E665", {"start": v(-158.13, 85.46) * mm, "end": v(-164.84, 68.4) * mm});
            skLineSegment(sketch, "E666", {"start": v(-164.84, 68.4) * mm, "end": v(-166.99, 68.4) * mm});
            skLineSegment(sketch, "E667", {"start": v(-91.16, -14.68) * mm, "end": v(-82.74, 6.7) * mm});
            skLineSegment(sketch, "E668", {"start": v(-82.74, 6.7) * mm, "end": v(-81.8, 6.7) * mm});
            skLineSegment(sketch, "E669", {"start": v(-81.8, 6.7) * mm, "end": v(-73.66, -14.68) * mm});
            skLineSegment(sketch, "E670", {"start": v(-73.66, -14.68) * mm, "end": v(-75.9, -14.68) * mm});
            skLineSegment(sketch, "E671", {"start": v(-75.9, -14.68) * mm, "end": v(-77.93, -9.37) * mm});
            skLineSegment(sketch, "E672", {"start": v(-77.93, -9.37) * mm, "end": v(-82.97, -9.37) * mm});
            skLineSegment(sketch, "E673", {"start": v(-82.97, -9.37) * mm, "end": v(-82.97, -7.37) * mm});
            skLineSegment(sketch, "E674", {"start": v(-82.97, -7.37) * mm, "end": v(-78.59, -7.37) * mm});
            skLineSegment(sketch, "E675", {"start": v(-78.59, -7.37) * mm, "end": v(-82.3, 2.37) * mm});
            skLineSegment(sketch, "E676", {"start": v(-82.3, 2.37) * mm, "end": v(-89, -14.68) * mm});
            skLineSegment(sketch, "E677", {"start": v(-89, -14.68) * mm, "end": v(-91.16, -14.68) * mm});
            skLineSegment(sketch, "E678", {"start": v(-87.74, 275.84) * mm, "end": v(-87.74, 297.34) * mm});
            skLineSegment(sketch, "E679", {"start": v(-87.74, 297.34) * mm, "end": v(-74.69, 297.34) * mm});
            skLineSegment(sketch, "E680", {"start": v(-74.69, 297.34) * mm, "end": v(-74.69, 295.34) * mm});
            skLineSegment(sketch, "E681", {"start": v(-74.69, 295.34) * mm, "end": v(-85.74, 295.34) * mm});
            skLineSegment(sketch, "E682", {"start": v(-85.74, 295.34) * mm, "end": v(-85.74, 287.07) * mm});
            skLineSegment(sketch, "E683", {"start": v(-85.74, 287.07) * mm, "end": v(-76.56, 287.07) * mm});
            skLineSegment(sketch, "E684", {"start": v(-76.56, 287.07) * mm, "end": v(-76.56, 285.07) * mm});
            skLineSegment(sketch, "E685", {"start": v(-76.56, 285.07) * mm, "end": v(-85.74, 285.07) * mm});
            skLineSegment(sketch, "E686", {"start": v(-85.74, 285.07) * mm, "end": v(-85.74, 275.84) * mm});
            skLineSegment(sketch, "E687", {"start": v(-85.74, 275.84) * mm, "end": v(-87.74, 275.84) * mm});
            skLineSegment(sketch, "E688", {"start": v(25.54, 275.81) * mm, "end": v(25.54, 297.31) * mm});
            skLineSegment(sketch, "E689", {"start": v(25.54, 297.31) * mm, "end": v(38.6, 297.31) * mm});
            skLineSegment(sketch, "E690", {"start": v(38.6, 297.31) * mm, "end": v(38.6, 295.31) * mm});
            skLineSegment(sketch, "E691", {"start": v(38.6, 295.31) * mm, "end": v(27.54, 295.31) * mm});
            skLineSegment(sketch, "E692", {"start": v(27.54, 295.31) * mm, "end": v(27.54, 287.05) * mm});
            skLineSegment(sketch, "E693", {"start": v(27.54, 287.05) * mm, "end": v(36.72, 287.05) * mm});
            skLineSegment(sketch, "E694", {"start": v(36.72, 287.05) * mm, "end": v(36.72, 285.05) * mm});
            skLineSegment(sketch, "E695", {"start": v(36.72, 285.05) * mm, "end": v(27.54, 285.05) * mm});
            skLineSegment(sketch, "E696", {"start": v(27.54, 285.05) * mm, "end": v(27.54, 275.81) * mm});
            skLineSegment(sketch, "E697", {"start": v(27.54, 275.81) * mm, "end": v(25.54, 275.81) * mm});
            skLineSegment(sketch, "E698", {"start": v(-87.85, 109.7) * mm, "end": v(-87.85, 131.18) * mm});
            skLineSegment(sketch, "E699", {"start": v(-87.85, 131.18) * mm, "end": v(-74.8, 131.18) * mm});
            skLineSegment(sketch, "E700", {"start": v(-74.8, 131.18) * mm, "end": v(-74.8, 129.18) * mm});
            skLineSegment(sketch, "E701", {"start": v(-74.8, 129.18) * mm, "end": v(-85.85, 129.18) * mm});
            skLineSegment(sketch, "E702", {"start": v(-85.85, 129.18) * mm, "end": v(-85.85, 120.93) * mm});
            skLineSegment(sketch, "E703", {"start": v(-85.85, 120.93) * mm, "end": v(-76.67, 120.93) * mm});
            skLineSegment(sketch, "E704", {"start": v(-76.67, 120.93) * mm, "end": v(-76.67, 118.93) * mm});
            skLineSegment(sketch, "E705", {"start": v(-76.67, 118.93) * mm, "end": v(-85.85, 118.93) * mm});
            skLineSegment(sketch, "E706", {"start": v(-85.85, 118.93) * mm, "end": v(-85.85, 109.7) * mm});
            skLineSegment(sketch, "E707", {"start": v(-85.85, 109.7) * mm, "end": v(-87.85, 109.7) * mm});
            skLineSegment(sketch, "E708", {"start": v(25.29, 109.92) * mm, "end": v(25.29, 131.4) * mm});
            skLineSegment(sketch, "E709", {"start": v(25.29, 131.4) * mm, "end": v(38.34, 131.4) * mm});
            skLineSegment(sketch, "E710", {"start": v(38.34, 131.4) * mm, "end": v(38.34, 129.4) * mm});
            skLineSegment(sketch, "E711", {"start": v(38.34, 129.4) * mm, "end": v(27.29, 129.4) * mm});
            skLineSegment(sketch, "E712", {"start": v(27.29, 129.4) * mm, "end": v(27.29, 121.15) * mm});
            skLineSegment(sketch, "E713", {"start": v(27.29, 121.15) * mm, "end": v(36.46, 121.15) * mm});
            skLineSegment(sketch, "E714", {"start": v(36.46, 121.15) * mm, "end": v(36.46, 119.15) * mm});
            skLineSegment(sketch, "E715", {"start": v(36.46, 119.15) * mm, "end": v(27.29, 119.15) * mm});
            skLineSegment(sketch, "E716", {"start": v(27.29, 119.15) * mm, "end": v(27.29, 109.92) * mm});
            skLineSegment(sketch, "E717", {"start": v(27.29, 109.92) * mm, "end": v(25.29, 109.92) * mm});
            skLineSegment(sketch, "E718", {"start": v(25.29, -56.75) * mm, "end": v(25.29, -35.26) * mm});
            skLineSegment(sketch, "E719", {"start": v(25.29, -35.26) * mm, "end": v(38.34, -35.26) * mm});
            skLineSegment(sketch, "E720", {"start": v(38.34, -35.26) * mm, "end": v(38.34, -37.26) * mm});
            skLineSegment(sketch, "E721", {"start": v(38.34, -37.26) * mm, "end": v(27.29, -37.26) * mm});
            skLineSegment(sketch, "E722", {"start": v(27.29, -37.26) * mm, "end": v(27.29, -45.51) * mm});
            skLineSegment(sketch, "E723", {"start": v(27.29, -45.51) * mm, "end": v(36.46, -45.51) * mm});
            skLineSegment(sketch, "E724", {"start": v(36.46, -45.51) * mm, "end": v(36.46, -47.51) * mm});
            skLineSegment(sketch, "E725", {"start": v(36.46, -47.51) * mm, "end": v(27.29, -47.51) * mm});
            skLineSegment(sketch, "E726", {"start": v(27.29, -47.51) * mm, "end": v(27.29, -56.75) * mm});
            skLineSegment(sketch, "E727", {"start": v(27.29, -56.75) * mm, "end": v(25.29, -56.75) * mm});
            skLineSegment(sketch, "E728.bottom", {"start": v(-48.68, 300.69) * mm, "end": v(-46.68, 300.69) * mm});
            skLineSegment(sketch, "E728.top", {"start": v(-48.68, 298.19) * mm, "end": v(-46.68, 298.19) * mm});
            skLineSegment(sketch, "E728.left", {"start": v(-48.68, 300.69) * mm, "end": v(-48.68, 298.19) * mm});
            skLineSegment(sketch, "E728.right", {"start": v(-46.68, 300.69) * mm, "end": v(-46.68, 298.19) * mm});
            skLineSegment(sketch, "E729.bottom", {"start": v(-42.62, 300.69) * mm, "end": v(-40.62, 300.69) * mm});
            skLineSegment(sketch, "E729.top", {"start": v(-42.62, 298.19) * mm, "end": v(-40.62, 298.19) * mm});
            skLineSegment(sketch, "E729.left", {"start": v(-42.62, 300.69) * mm, "end": v(-42.62, 298.19) * mm});
            skLineSegment(sketch, "E729.right", {"start": v(-40.62, 300.69) * mm, "end": v(-40.62, 298.19) * mm});
            skLineSegment(sketch, "E730", {"start": v(-52.02, 296.68) * mm, "end": v(-50.02, 296.68) * mm});
            skLineSegment(sketch, "E731", {"start": v(-50.02, 296.68) * mm, "end": v(-50.02, 282.44) * mm});
            skLineSegment(sketch, "E732", {"start": v(-52.02, 296.68) * mm, "end": v(-52.02, 282.44) * mm});
            skLineSegment(sketch, "E733", {"start": v(-39.5, 296.68) * mm, "end": v(-37.5, 296.68) * mm});
            skLineSegment(sketch, "E734", {"start": v(-37.5, 296.68) * mm, "end": v(-37.5, 282.44) * mm});
            skArc(sketch, "E735", {"start": v(-50.02, 282.44) * mm, "mid": v(-44.76, 277.18) * mm, "end": v(-39.5, 282.44) * mm});
            skArc(sketch, "E736", {"start": v(-52.02, 282.44) * mm, "mid": v(-44.76, 275.18) * mm, "end": v(-37.5, 282.44) * mm});
            skLineSegment(sketch, "E737", {"start": v(-14.66, 297.31) * mm, "end": v(-14.66, 275.81) * mm});
            skLineSegment(sketch, "E738", {"start": v(-14.66, 275.81) * mm, "end": v(-12.66, 275.81) * mm});
            skLineSegment(sketch, "E739", {"start": v(-12.66, 275.81) * mm, "end": v(-12.66, 293.6) * mm});
            skLineSegment(sketch, "E740", {"start": v(-12.66, 293.6) * mm, "end": v(-1.32, 275.81) * mm});
            skLineSegment(sketch, "E741", {"start": v(-1.32, 275.81) * mm, "end": v(0.68, 275.81) * mm});
            skLineSegment(sketch, "E742", {"start": v(0.68, 275.81) * mm, "end": v(0.68, 297.4) * mm});
            skLineSegment(sketch, "E743", {"start": v(0.68, 297.4) * mm, "end": v(-1.32, 297.4) * mm});
            skLineSegment(sketch, "E744", {"start": v(-1.32, 297.4) * mm, "end": v(-1.32, 279.53) * mm});
            skLineSegment(sketch, "E745", {"start": v(-1.32, 279.53) * mm, "end": v(-12.66, 297.31) * mm});
            skLineSegment(sketch, "E746", {"start": v(-12.66, 297.31) * mm, "end": v(-14.66, 297.31) * mm});
            skLineSegment(sketch, "E747", {"start": v(-241.31, 255.68) * mm, "end": v(-241.31, 234.18) * mm});
            skLineSegment(sketch, "E748", {"start": v(-241.31, 234.18) * mm, "end": v(-239.31, 234.18) * mm});
            skLineSegment(sketch, "E749", {"start": v(-239.31, 234.18) * mm, "end": v(-239.31, 251.96) * mm});
            skLineSegment(sketch, "E750", {"start": v(-239.31, 251.96) * mm, "end": v(-227.97, 234.18) * mm});
            skLineSegment(sketch, "E751", {"start": v(-227.97, 234.18) * mm, "end": v(-225.97, 234.18) * mm});
            skLineSegment(sketch, "E752", {"start": v(-225.97, 234.18) * mm, "end": v(-225.97, 255.76) * mm});
            skLineSegment(sketch, "E753", {"start": v(-225.97, 255.76) * mm, "end": v(-227.97, 255.76) * mm});
            skLineSegment(sketch, "E754", {"start": v(-227.97, 255.76) * mm, "end": v(-227.97, 237.9) * mm});
            skLineSegment(sketch, "E755", {"start": v(-227.97, 237.9) * mm, "end": v(-239.31, 255.68) * mm});
            skLineSegment(sketch, "E756", {"start": v(-239.31, 255.68) * mm, "end": v(-241.31, 255.68) * mm});
            skLineSegment(sketch, "E757", {"start": v(-90.13, 255.68) * mm, "end": v(-90.13, 234.18) * mm});
            skLineSegment(sketch, "E758", {"start": v(-90.13, 234.18) * mm, "end": v(-88.13, 234.18) * mm});
            skLineSegment(sketch, "E759", {"start": v(-88.13, 234.18) * mm, "end": v(-88.13, 251.96) * mm});
            skLineSegment(sketch, "E760", {"start": v(-88.13, 251.96) * mm, "end": v(-76.8, 234.18) * mm});
            skLineSegment(sketch, "E761", {"start": v(-76.8, 234.18) * mm, "end": v(-74.8, 234.18) * mm});
            skLineSegment(sketch, "E762", {"start": v(-74.8, 234.18) * mm, "end": v(-74.8, 255.76) * mm});
            skLineSegment(sketch, "E763", {"start": v(-74.8, 255.76) * mm, "end": v(-76.8, 255.76) * mm});
            skLineSegment(sketch, "E764", {"start": v(-76.8, 255.76) * mm, "end": v(-76.8, 237.9) * mm});
            skLineSegment(sketch, "E765", {"start": v(-76.8, 237.9) * mm, "end": v(-88.13, 255.68) * mm});
            skLineSegment(sketch, "E766", {"start": v(-88.13, 255.68) * mm, "end": v(-90.13, 255.68) * mm});
            skLineSegment(sketch, "E767", {"start": v(-90.2, 172.66) * mm, "end": v(-90.2, 151.07) * mm});
            skLineSegment(sketch, "E768", {"start": v(-90.2, 151.07) * mm, "end": v(-88.2, 151.07) * mm});
            skLineSegment(sketch, "E769", {"start": v(-88.2, 151.07) * mm, "end": v(-88.2, 168.94) * mm});
            skLineSegment(sketch, "E770", {"start": v(-88.2, 168.94) * mm, "end": v(-76.8, 151.07) * mm});
            skLineSegment(sketch, "E771", {"start": v(-76.8, 151.07) * mm, "end": v(-74.8, 151.07) * mm});
            skLineSegment(sketch, "E772", {"start": v(-74.8, 151.07) * mm, "end": v(-74.8, 172.66) * mm});
            skLineSegment(sketch, "E773", {"start": v(-74.8, 172.66) * mm, "end": v(-76.8, 172.66) * mm});
            skLineSegment(sketch, "E774", {"start": v(-76.8, 172.66) * mm, "end": v(-76.8, 154.8) * mm});
            skLineSegment(sketch, "E775", {"start": v(-76.8, 154.8) * mm, "end": v(-88.2, 172.66) * mm});
            skLineSegment(sketch, "E776", {"start": v(-88.2, 172.66) * mm, "end": v(-90.2, 172.66) * mm});
            skLineSegment(sketch, "E777", {"start": v(-14.5, 131.23) * mm, "end": v(-14.5, 109.65) * mm});
            skLineSegment(sketch, "E778", {"start": v(-14.5, 109.65) * mm, "end": v(-12.5, 109.65) * mm});
            skLineSegment(sketch, "E779", {"start": v(-12.5, 109.65) * mm, "end": v(-12.5, 127.51) * mm});
            skLineSegment(sketch, "E780", {"start": v(-12.5, 127.51) * mm, "end": v(-1.1, 109.65) * mm});
            skLineSegment(sketch, "E781", {"start": v(-1.1, 109.65) * mm, "end": v(0.9, 109.65) * mm});
            skLineSegment(sketch, "E782", {"start": v(0.9, 109.65) * mm, "end": v(0.9, 131.23) * mm});
            skLineSegment(sketch, "E783", {"start": v(0.9, 131.23) * mm, "end": v(-1.1, 131.23) * mm});
            skLineSegment(sketch, "E784", {"start": v(-1.1, 131.23) * mm, "end": v(-1.1, 113.37) * mm});
            skLineSegment(sketch, "E785", {"start": v(-1.1, 113.37) * mm, "end": v(-12.5, 131.23) * mm});
            skLineSegment(sketch, "E786", {"start": v(-12.5, 131.23) * mm, "end": v(-14.5, 131.23) * mm});
            skLineSegment(sketch, "E787", {"start": v(-278.93, 89.79) * mm, "end": v(-278.93, 68.2) * mm});
            skLineSegment(sketch, "E788", {"start": v(-278.93, 68.2) * mm, "end": v(-276.93, 68.2) * mm});
            skLineSegment(sketch, "E789", {"start": v(-276.93, 68.2) * mm, "end": v(-276.93, 86.07) * mm});
            skLineSegment(sketch, "E790", {"start": v(-276.93, 86.07) * mm, "end": v(-265.54, 68.2) * mm});
            skLineSegment(sketch, "E791", {"start": v(-265.54, 68.2) * mm, "end": v(-263.54, 68.2) * mm});
            skLineSegment(sketch, "E792", {"start": v(-263.54, 68.2) * mm, "end": v(-263.54, 89.79) * mm});
            skLineSegment(sketch, "E793", {"start": v(-263.54, 89.79) * mm, "end": v(-265.54, 89.79) * mm});
            skLineSegment(sketch, "E794", {"start": v(-265.54, 89.79) * mm, "end": v(-265.54, 71.92) * mm});
            skLineSegment(sketch, "E795", {"start": v(-265.54, 71.92) * mm, "end": v(-276.93, 89.79) * mm});
            skLineSegment(sketch, "E796", {"start": v(-276.93, 89.79) * mm, "end": v(-278.93, 89.79) * mm});
            skLineSegment(sketch, "E797", {"start": v(-165.69, 7) * mm, "end": v(-165.69, -14.58) * mm});
            skLineSegment(sketch, "E798", {"start": v(-165.69, -14.58) * mm, "end": v(-163.69, -14.58) * mm});
            skLineSegment(sketch, "E799", {"start": v(-163.69, -14.58) * mm, "end": v(-163.69, 3.28) * mm});
            skLineSegment(sketch, "E800", {"start": v(-163.69, 3.28) * mm, "end": v(-152.3, -14.58) * mm});
            skLineSegment(sketch, "E801", {"start": v(-152.3, -14.58) * mm, "end": v(-150.3, -14.58) * mm});
            skLineSegment(sketch, "E802", {"start": v(-150.3, -14.58) * mm, "end": v(-150.3, 7) * mm});
            skLineSegment(sketch, "E803", {"start": v(-150.3, 7) * mm, "end": v(-152.3, 7) * mm});
            skLineSegment(sketch, "E804", {"start": v(-152.3, 7) * mm, "end": v(-152.3, -10.86) * mm});
            skLineSegment(sketch, "E805", {"start": v(-152.3, -10.86) * mm, "end": v(-163.69, 7) * mm});
            skLineSegment(sketch, "E806", {"start": v(-163.69, 7) * mm, "end": v(-165.69, 7) * mm});
            skLineSegment(sketch, "E807", {"start": v(-165.76, -34.8) * mm, "end": v(-165.76, -56.38) * mm});
            skLineSegment(sketch, "E808", {"start": v(-165.76, -56.38) * mm, "end": v(-163.76, -56.38) * mm});
            skLineSegment(sketch, "E809", {"start": v(-163.76, -56.38) * mm, "end": v(-163.76, -38.52) * mm});
            skLineSegment(sketch, "E810", {"start": v(-163.76, -38.52) * mm, "end": v(-152.37, -56.38) * mm});
            skLineSegment(sketch, "E811", {"start": v(-152.37, -56.38) * mm, "end": v(-150.37, -56.38) * mm});
            skLineSegment(sketch, "E812", {"start": v(-150.37, -56.38) * mm, "end": v(-150.37, -34.8) * mm});
            skLineSegment(sketch, "E813", {"start": v(-150.37, -34.8) * mm, "end": v(-152.37, -34.8) * mm});
            skLineSegment(sketch, "E814", {"start": v(-152.37, -34.8) * mm, "end": v(-152.37, -52.66) * mm});
            skLineSegment(sketch, "E815", {"start": v(-152.37, -52.66) * mm, "end": v(-163.76, -34.8) * mm});
            skLineSegment(sketch, "E816", {"start": v(-163.76, -34.8) * mm, "end": v(-165.76, -34.8) * mm});
            skLineSegment(sketch, "E817", {"start": v(-241.22, -76.22) * mm, "end": v(-241.22, -97.8) * mm});
            skLineSegment(sketch, "E818", {"start": v(-241.22, -97.8) * mm, "end": v(-239.22, -97.8) * mm});
            skLineSegment(sketch, "E819", {"start": v(-239.22, -97.8) * mm, "end": v(-239.22, -79.94) * mm});
            skLineSegment(sketch, "E820", {"start": v(-239.22, -79.94) * mm, "end": v(-227.82, -97.8) * mm});
            skLineSegment(sketch, "E821", {"start": v(-227.82, -97.8) * mm, "end": v(-225.82, -97.8) * mm});
            skLineSegment(sketch, "E822", {"start": v(-225.82, -97.8) * mm, "end": v(-225.82, -76.22) * mm});
            skLineSegment(sketch, "E823", {"start": v(-225.82, -76.22) * mm, "end": v(-227.82, -76.22) * mm});
            skLineSegment(sketch, "E824", {"start": v(-227.82, -76.22) * mm, "end": v(-227.82, -94.09) * mm});
            skLineSegment(sketch, "E825", {"start": v(-227.82, -94.09) * mm, "end": v(-239.22, -76.22) * mm});
            skLineSegment(sketch, "E826", {"start": v(-239.22, -76.22) * mm, "end": v(-241.22, -76.22) * mm});
            skLineSegment(sketch, "E827", {"start": v(-127.82, -76.18) * mm, "end": v(-127.82, -97.77) * mm});
            skLineSegment(sketch, "E828", {"start": v(-127.82, -97.77) * mm, "end": v(-125.82, -97.77) * mm});
            skLineSegment(sketch, "E829", {"start": v(-125.82, -97.77) * mm, "end": v(-125.82, -79.9) * mm});
            skLineSegment(sketch, "E830", {"start": v(-125.82, -79.9) * mm, "end": v(-114.43, -97.77) * mm});
            skLineSegment(sketch, "E831", {"start": v(-114.43, -97.77) * mm, "end": v(-112.43, -97.77) * mm});
            skLineSegment(sketch, "E832", {"start": v(-112.43, -97.77) * mm, "end": v(-112.43, -76.18) * mm});
            skLineSegment(sketch, "E833", {"start": v(-112.43, -76.18) * mm, "end": v(-114.43, -76.18) * mm});
            skLineSegment(sketch, "E834", {"start": v(-114.43, -76.18) * mm, "end": v(-114.43, -94.05) * mm});
            skLineSegment(sketch, "E835", {"start": v(-114.43, -94.05) * mm, "end": v(-125.82, -76.18) * mm});
            skLineSegment(sketch, "E836", {"start": v(-125.82, -76.18) * mm, "end": v(-127.82, -76.18) * mm});
            skLineSegment(sketch, "E837", {"start": v(-189.77, 234.06) * mm, "end": v(-203, 234.06) * mm});
            skLineSegment(sketch, "E838", {"start": v(-203, 234.06) * mm, "end": v(-203, 236.06) * mm});
            skLineSegment(sketch, "E839", {"start": v(-203, 236.06) * mm, "end": v(-192.7, 252.31) * mm});
            skLineSegment(sketch, "E840", {"start": v(-192.7, 252.31) * mm, "end": v(-192.7, 253.56) * mm});
            skLineSegment(sketch, "E841", {"start": v(-192.7, 253.56) * mm, "end": v(-202.49, 253.56) * mm});
            skLineSegment(sketch, "E842", {"start": v(-202.49, 253.56) * mm, "end": v(-202.49, 255.56) * mm});
            skLineSegment(sketch, "E843", {"start": v(-202.49, 255.56) * mm, "end": v(-189.55, 255.56) * mm});
            skLineSegment(sketch, "E844", {"start": v(-189.55, 255.56) * mm, "end": v(-189.55, 253.56) * mm});
            skLineSegment(sketch, "E845", {"start": v(-189.55, 253.56) * mm, "end": v(-200.63, 236.06) * mm});
            skLineSegment(sketch, "E846", {"start": v(-200.63, 236.06) * mm, "end": v(-189.77, 236.06) * mm});
            skLineSegment(sketch, "E847", {"start": v(-189.77, 236.06) * mm, "end": v(-189.77, 234.06) * mm});
            skLineSegment(sketch, "E848", {"start": v(-38.65, 233.81) * mm, "end": v(-51.87, 233.81) * mm});
            skLineSegment(sketch, "E849", {"start": v(-51.87, 233.81) * mm, "end": v(-51.87, 235.81) * mm});
            skLineSegment(sketch, "E850", {"start": v(-51.87, 235.81) * mm, "end": v(-41.58, 251.31) * mm});
            skLineSegment(sketch, "E851", {"start": v(-41.58, 251.31) * mm, "end": v(-41.58, 253.31) * mm});
            skLineSegment(sketch, "E852", {"start": v(-41.58, 253.31) * mm, "end": v(-51.36, 253.31) * mm});
            skLineSegment(sketch, "E853", {"start": v(-51.36, 253.31) * mm, "end": v(-51.36, 255.31) * mm});
            skLineSegment(sketch, "E854", {"start": v(-51.36, 255.31) * mm, "end": v(-37.85, 255.31) * mm});
            skLineSegment(sketch, "E855", {"start": v(-37.85, 255.31) * mm, "end": v(-37.85, 253.31) * mm});
            skLineSegment(sketch, "E856", {"start": v(-37.85, 253.31) * mm, "end": v(-49.47, 235.81) * mm});
            skLineSegment(sketch, "E857", {"start": v(-49.47, 235.81) * mm, "end": v(-38.65, 235.81) * mm});
            skLineSegment(sketch, "E858", {"start": v(-38.65, 235.81) * mm, "end": v(-38.65, 233.81) * mm});
            skLineSegment(sketch, "E859", {"start": v(-113.33, -56.19) * mm, "end": v(-126.56, -56.19) * mm});
            skLineSegment(sketch, "E860", {"start": v(-126.56, -56.19) * mm, "end": v(-126.56, -54.19) * mm});
            skLineSegment(sketch, "E861", {"start": v(-126.56, -54.19) * mm, "end": v(-116.26, -37.94) * mm});
            skLineSegment(sketch, "E862", {"start": v(-116.26, -37.94) * mm, "end": v(-116.26, -37.13) * mm});
            skLineSegment(sketch, "E863", {"start": v(-116.26, -37.13) * mm, "end": v(-126.04, -37.13) * mm});
            skLineSegment(sketch, "E864", {"start": v(-126.04, -37.13) * mm, "end": v(-126.04, -35.13) * mm});
            skLineSegment(sketch, "E865", {"start": v(-126.04, -35.13) * mm, "end": v(-113.39, -35.13) * mm});
            skLineSegment(sketch, "E866", {"start": v(-113.39, -35.13) * mm, "end": v(-113.39, -37.13) * mm});
            skLineSegment(sketch, "E867", {"start": v(-113.39, -37.13) * mm, "end": v(-124.19, -54.19) * mm});
            skLineSegment(sketch, "E868", {"start": v(-124.19, -54.19) * mm, "end": v(-113.33, -54.19) * mm});
            skLineSegment(sketch, "E869", {"start": v(-113.33, -54.19) * mm, "end": v(-113.33, -56.19) * mm});
            skLineSegment(sketch, "E870", {"start": v(-340.34, -97.4) * mm, "end": v(-353.56, -97.4) * mm});
            skLineSegment(sketch, "E871", {"start": v(-353.56, -97.4) * mm, "end": v(-353.56, -95.4) * mm});
            skLineSegment(sketch, "E872", {"start": v(-353.56, -95.4) * mm, "end": v(-343.27, -79.15) * mm});
            skLineSegment(sketch, "E873", {"start": v(-343.27, -79.15) * mm, "end": v(-343.27, -78.34) * mm});
            skLineSegment(sketch, "E874", {"start": v(-343.27, -78.34) * mm, "end": v(-353.05, -78.34) * mm});
            skLineSegment(sketch, "E875", {"start": v(-353.05, -78.34) * mm, "end": v(-353.05, -76.34) * mm});
            skLineSegment(sketch, "E876", {"start": v(-353.05, -76.34) * mm, "end": v(-340.4, -76.34) * mm});
            skLineSegment(sketch, "E877", {"start": v(-340.4, -76.34) * mm, "end": v(-340.4, -78.34) * mm});
            skLineSegment(sketch, "E878", {"start": v(-340.4, -78.34) * mm, "end": v(-351.2, -95.4) * mm});
            skLineSegment(sketch, "E879", {"start": v(-351.2, -95.4) * mm, "end": v(-340.34, -95.4) * mm});
            skLineSegment(sketch, "E880", {"start": v(-340.34, -95.4) * mm, "end": v(-340.34, -97.4) * mm});
            skLineSegment(sketch, "E881", {"start": v(-340.2, 233.87) * mm, "end": v(-353.42, 233.87) * mm});
            skLineSegment(sketch, "E882", {"start": v(-353.42, 233.87) * mm, "end": v(-353.42, 235.87) * mm});
            skLineSegment(sketch, "E883", {"start": v(-353.42, 235.87) * mm, "end": v(-343.13, 252.12) * mm});
            skLineSegment(sketch, "E884", {"start": v(-343.13, 252.12) * mm, "end": v(-343.13, 253.37) * mm});
            skLineSegment(sketch, "E885", {"start": v(-343.13, 253.37) * mm, "end": v(-352.9, 253.37) * mm});
            skLineSegment(sketch, "E886", {"start": v(-352.9, 253.37) * mm, "end": v(-352.9, 255.37) * mm});
            skLineSegment(sketch, "E887", {"start": v(-352.9, 255.37) * mm, "end": v(-339.97, 255.37) * mm});
            skLineSegment(sketch, "E888", {"start": v(-339.97, 255.37) * mm, "end": v(-339.97, 253.37) * mm});
            skLineSegment(sketch, "E889", {"start": v(-339.97, 253.37) * mm, "end": v(-351.05, 235.87) * mm});
            skLineSegment(sketch, "E890", {"start": v(-351.05, 235.87) * mm, "end": v(-340.2, 235.87) * mm});
            skLineSegment(sketch, "E891", {"start": v(-340.2, 235.87) * mm, "end": v(-340.2, 233.87) * mm});
            skLineSegment(sketch, "E892", {"start": v(-278.65, 234.06) * mm, "end": v(-278.65, 255.56) * mm});
            skLineSegment(sketch, "E893", {"start": v(-278.65, 255.56) * mm, "end": v(-276.65, 255.56) * mm});
            skLineSegment(sketch, "E894", {"start": v(-276.65, 255.56) * mm, "end": v(-276.65, 245.78) * mm});
            skLineSegment(sketch, "E895", {"start": v(-276.65, 245.78) * mm, "end": v(-266.45, 245.78) * mm});
            skLineSegment(sketch, "E896", {"start": v(-266.45, 245.78) * mm, "end": v(-266.45, 255.56) * mm});
            skLineSegment(sketch, "E897", {"start": v(-266.45, 255.56) * mm, "end": v(-264.45, 255.56) * mm});
            skLineSegment(sketch, "E898", {"start": v(-264.45, 255.56) * mm, "end": v(-264.45, 234.06) * mm});
            skLineSegment(sketch, "E899", {"start": v(-264.45, 234.06) * mm, "end": v(-266.45, 234.06) * mm});
            skLineSegment(sketch, "E900", {"start": v(-266.45, 234.06) * mm, "end": v(-266.45, 243.78) * mm});
            skLineSegment(sketch, "E901", {"start": v(-266.45, 243.78) * mm, "end": v(-276.65, 243.78) * mm});
            skLineSegment(sketch, "E902", {"start": v(-276.65, 243.78) * mm, "end": v(-276.65, 234.06) * mm});
            skLineSegment(sketch, "E903", {"start": v(-276.65, 234.06) * mm, "end": v(-278.65, 234.06) * mm});
            skLineSegment(sketch, "E904", {"start": v(23.58, 151.2) * mm, "end": v(23.58, 172.59) * mm});
            skLineSegment(sketch, "E905", {"start": v(23.58, 172.59) * mm, "end": v(25.58, 172.59) * mm});
            skLineSegment(sketch, "E906", {"start": v(25.58, 172.59) * mm, "end": v(25.58, 162.92) * mm});
            skLineSegment(sketch, "E907", {"start": v(25.58, 162.92) * mm, "end": v(35.78, 162.92) * mm});
            skLineSegment(sketch, "E908", {"start": v(35.78, 162.92) * mm, "end": v(35.78, 172.59) * mm});
            skLineSegment(sketch, "E909", {"start": v(35.78, 172.59) * mm, "end": v(37.78, 172.59) * mm});
            skLineSegment(sketch, "E910", {"start": v(37.78, 172.59) * mm, "end": v(37.78, 151.2) * mm});
            skLineSegment(sketch, "E911", {"start": v(37.78, 151.2) * mm, "end": v(35.78, 151.2) * mm});
            skLineSegment(sketch, "E912", {"start": v(35.78, 151.2) * mm, "end": v(35.78, 160.92) * mm});
            skLineSegment(sketch, "E913", {"start": v(35.78, 160.92) * mm, "end": v(25.58, 160.92) * mm});
            skLineSegment(sketch, "E914", {"start": v(25.58, 160.92) * mm, "end": v(25.58, 151.2) * mm});
            skLineSegment(sketch, "E915", {"start": v(25.58, 151.2) * mm, "end": v(23.58, 151.2) * mm});
            skLineSegment(sketch, "E916", {"start": v(-14.2, -97.57) * mm, "end": v(-14.2, -76.18) * mm});
            skLineSegment(sketch, "E917", {"start": v(-14.2, -76.18) * mm, "end": v(-12.2, -76.18) * mm});
            skLineSegment(sketch, "E918", {"start": v(-12.2, -76.18) * mm, "end": v(-12.2, -85.85) * mm});
            skLineSegment(sketch, "E919", {"start": v(-12.2, -85.85) * mm, "end": v(-2, -85.85) * mm});
            skLineSegment(sketch, "E920", {"start": v(-2, -85.85) * mm, "end": v(-2, -76.18) * mm});
            skLineSegment(sketch, "E921", {"start": v(-2, -76.18) * mm, "end": v(0, -76.18) * mm});
            skLineSegment(sketch, "E922", {"start": v(0, -76.18) * mm, "end": v(0, -97.57) * mm});
            skLineSegment(sketch, "E923", {"start": v(0, -97.57) * mm, "end": v(-2, -97.57) * mm});
            skLineSegment(sketch, "E924", {"start": v(-2, -97.57) * mm, "end": v(-2, -87.85) * mm});
            skLineSegment(sketch, "E925", {"start": v(-2, -87.85) * mm, "end": v(-12.2, -87.85) * mm});
            skLineSegment(sketch, "E926", {"start": v(-12.2, -87.85) * mm, "end": v(-12.2, -97.57) * mm});
            skLineSegment(sketch, "E927", {"start": v(-12.2, -97.57) * mm, "end": v(-14.2, -97.57) * mm});
            skLineSegment(sketch, "E928", {"start": v(-240.51, -14.59) * mm, "end": v(-240.51, 6.8) * mm});
            skLineSegment(sketch, "E929", {"start": v(-240.51, 6.8) * mm, "end": v(-238.51, 6.8) * mm});
            skLineSegment(sketch, "E930", {"start": v(-238.51, 6.8) * mm, "end": v(-238.51, -2.87) * mm});
            skLineSegment(sketch, "E931", {"start": v(-238.51, -2.87) * mm, "end": v(-228.31, -2.87) * mm});
            skLineSegment(sketch, "E932", {"start": v(-228.31, -2.87) * mm, "end": v(-228.31, 6.8) * mm});
            skLineSegment(sketch, "E933", {"start": v(-228.31, 6.8) * mm, "end": v(-226.31, 6.8) * mm});
            skLineSegment(sketch, "E934", {"start": v(-226.31, 6.8) * mm, "end": v(-226.31, -14.59) * mm});
            skLineSegment(sketch, "E935", {"start": v(-226.31, -14.59) * mm, "end": v(-228.31, -14.59) * mm});
            skLineSegment(sketch, "E936", {"start": v(-228.31, -14.59) * mm, "end": v(-228.31, -4.87) * mm});
            skLineSegment(sketch, "E937", {"start": v(-228.31, -4.87) * mm, "end": v(-238.51, -4.87) * mm});
            skLineSegment(sketch, "E938", {"start": v(-238.51, -4.87) * mm, "end": v(-238.51, -14.59) * mm});
            skLineSegment(sketch, "E939", {"start": v(-238.51, -14.59) * mm, "end": v(-240.51, -14.59) * mm});
            skLineSegment(sketch, "E940", {"start": v(-278.5, -97.36) * mm, "end": v(-278.5, -75.98) * mm});
            skLineSegment(sketch, "E941", {"start": v(-278.5, -75.98) * mm, "end": v(-276.5, -75.98) * mm});
            skLineSegment(sketch, "E942", {"start": v(-276.5, -75.98) * mm, "end": v(-276.5, -85.65) * mm});
            skLineSegment(sketch, "E943", {"start": v(-276.5, -85.65) * mm, "end": v(-266.3, -85.65) * mm});
            skLineSegment(sketch, "E944", {"start": v(-266.3, -85.65) * mm, "end": v(-266.3, -75.98) * mm});
            skLineSegment(sketch, "E945", {"start": v(-266.3, -75.98) * mm, "end": v(-264.3, -75.98) * mm});
            skLineSegment(sketch, "E946", {"start": v(-264.3, -75.98) * mm, "end": v(-264.3, -97.36) * mm});
            skLineSegment(sketch, "E947", {"start": v(-264.3, -97.36) * mm, "end": v(-266.3, -97.36) * mm});
            skLineSegment(sketch, "E948", {"start": v(-266.3, -97.36) * mm, "end": v(-266.3, -87.65) * mm});
            skLineSegment(sketch, "E949", {"start": v(-266.3, -87.65) * mm, "end": v(-276.5, -87.65) * mm});
            skLineSegment(sketch, "E950", {"start": v(-276.5, -87.65) * mm, "end": v(-276.5, -97.36) * mm});
            skLineSegment(sketch, "E951", {"start": v(-276.5, -97.36) * mm, "end": v(-278.5, -97.36) * mm});
            skLineSegment(sketch, "E952", {"start": v(-169.9, 255.68) * mm, "end": v(-167.84, 255.68) * mm});
            skLineSegment(sketch, "E953", {"start": v(-167.84, 255.68) * mm, "end": v(-163.67, 238.2) * mm});
            skLineSegment(sketch, "E954", {"start": v(-163.67, 238.2) * mm, "end": v(-158.34, 255.68) * mm});
            skLineSegment(sketch, "E955", {"start": v(-158.34, 255.68) * mm, "end": v(-157.09, 255.68) * mm});
            skLineSegment(sketch, "E956", {"start": v(-157.09, 255.68) * mm, "end": v(-152.5, 238.2) * mm});
            skLineSegment(sketch, "E957", {"start": v(-152.5, 238.2) * mm, "end": v(-148.07, 255.68) * mm});
            skLineSegment(sketch, "E958", {"start": v(-148.07, 255.68) * mm, "end": v(-146, 255.68) * mm});
            skLineSegment(sketch, "E959", {"start": v(-146, 255.68) * mm, "end": v(-151.47, 234.18) * mm});
            skLineSegment(sketch, "E960", {"start": v(-151.47, 234.18) * mm, "end": v(-153.52, 234.18) * mm});
            skLineSegment(sketch, "E961", {"start": v(-153.52, 234.18) * mm, "end": v(-157.81, 250.56) * mm});
            skLineSegment(sketch, "E962", {"start": v(-157.81, 250.56) * mm, "end": v(-162.8, 234.18) * mm});
            skLineSegment(sketch, "E963", {"start": v(-162.8, 234.18) * mm, "end": v(-164.77, 234.18) * mm});
            skLineSegment(sketch, "E964", {"start": v(-164.77, 234.18) * mm, "end": v(-169.9, 255.68) * mm});
            skLineSegment(sketch, "E965", {"start": v(-94.27, -35.19) * mm, "end": v(-92.22, -35.19) * mm});
            skLineSegment(sketch, "E966", {"start": v(-92.22, -35.19) * mm, "end": v(-88.2, -52.04) * mm});
            skLineSegment(sketch, "E967", {"start": v(-88.2, -52.04) * mm, "end": v(-83.06, -35.19) * mm});
            skLineSegment(sketch, "E968", {"start": v(-83.06, -35.19) * mm, "end": v(-81.46, -35.19) * mm});
            skLineSegment(sketch, "E969", {"start": v(-81.46, -35.19) * mm, "end": v(-77.04, -52.04) * mm});
            skLineSegment(sketch, "E970", {"start": v(-77.04, -52.04) * mm, "end": v(-72.76, -35.19) * mm});
            skLineSegment(sketch, "E971", {"start": v(-72.76, -35.19) * mm, "end": v(-70.7, -35.19) * mm});
            skLineSegment(sketch, "E972", {"start": v(-70.7, -35.19) * mm, "end": v(-76, -56.06) * mm});
            skLineSegment(sketch, "E973", {"start": v(-76, -56.06) * mm, "end": v(-78.05, -56.06) * mm});
            skLineSegment(sketch, "E974", {"start": v(-78.05, -56.06) * mm, "end": v(-82.34, -39.69) * mm});
            skLineSegment(sketch, "E975", {"start": v(-82.34, -39.69) * mm, "end": v(-87.34, -56.06) * mm});
            skLineSegment(sketch, "E976", {"start": v(-87.34, -56.06) * mm, "end": v(-89.3, -56.06) * mm});
            skLineSegment(sketch, "E977", {"start": v(-89.3, -56.06) * mm, "end": v(-94.27, -35.19) * mm});
            skLineSegment(sketch, "E978", {"start": v(-353.27, 200) * mm, "end": v(-353.27, 213.83) * mm});
            skLineSegment(sketch, "E979", {"start": v(-353.27, 213.83) * mm, "end": v(-345.7, 213.83) * mm});
            skLineSegment(sketch, "E980", {"start": v(-353.27, 200) * mm, "end": v(-351.27, 200) * mm});
            skLineSegment(sketch, "E981", {"start": v(-351.27, 200) * mm, "end": v(-351.27, 211.83) * mm});
            skLineSegment(sketch, "E982", {"start": v(-351.27, 211.83) * mm, "end": v(-345.7, 211.83) * mm});
            skLineSegment(sketch, "E983", {"start": v(-353.27, 194.83) * mm, "end": v(-353.27, 192.7) * mm});
            skLineSegment(sketch, "E984", {"start": v(-353.27, 192.7) * mm, "end": v(-346.36, 192.7) * mm});
            skLineSegment(sketch, "E985", {"start": v(-353.27, 194.83) * mm, "end": v(-346.36, 194.83) * mm});
            skArc(sketch, "E986", {"start": v(-345.7, 211.83) * mm, "mid": v(-342.45, 210.51) * mm, "end": v(-341, 207.31) * mm});
            skArc(sketch, "E987", {"start": v(-345.7, 213.83) * mm, "mid": v(-341.03, 211.93) * mm, "end": v(-339, 207.31) * mm});
            skArc(sketch, "E988", {"start": v(-346.36, 194.83) * mm, "mid": v(-342.64, 196.33) * mm, "end": v(-341, 200) * mm});
            skArc(sketch, "E989", {"start": v(-346.36, 192.7) * mm, "mid": v(-341.18, 194.83) * mm, "end": v(-339, 200) * mm});
            skLineSegment(sketch, "E990", {"start": v(-341, 207.31) * mm, "end": v(-341, 200) * mm});
            skLineSegment(sketch, "E991", {"start": v(-339, 207.31) * mm, "end": v(-339, 200) * mm});
            skArc(sketch, "E992", {"start": v(-306.27, 204.14) * mm, "mid": v(-303.3, 208.32) * mm, "end": v(-307.13, 211.75) * mm});
            skArc(sketch, "E993", {"start": v(-306.07, 202.14) * mm, "mid": v(-301.3, 208.43) * mm, "end": v(-307.13, 213.75) * mm});
            skLineSegment(sketch, "E994", {"start": v(-307.13, 213.75) * mm, "end": v(-315.57, 213.75) * mm});
            skLineSegment(sketch, "E995", {"start": v(-315.57, 213.75) * mm, "end": v(-315.57, 211.75) * mm});
            skLineSegment(sketch, "E996", {"start": v(-315.57, 211.75) * mm, "end": v(-307.13, 211.75) * mm});
            skLineSegment(sketch, "E997", {"start": v(-306.27, 204.14) * mm, "end": v(-315.57, 204.14) * mm});
            skLineSegment(sketch, "E998", {"start": v(-315.57, 204.14) * mm, "end": v(-315.57, 192.74) * mm});
            skLineSegment(sketch, "E999", {"start": v(-315.57, 192.74) * mm, "end": v(-313.57, 192.74) * mm});
            skLineSegment(sketch, "E1000", {"start": v(-313.57, 192.74) * mm, "end": v(-313.57, 202.14) * mm});
            skLineSegment(sketch, "E1001", {"start": v(-313.57, 202.14) * mm, "end": v(-308.07, 202.14) * mm});
            skLineSegment(sketch, "E1002", {"start": v(-308.07, 202.14) * mm, "end": v(-302.8, 192.6) * mm});
            skLineSegment(sketch, "E1003", {"start": v(-302.8, 192.6) * mm, "end": v(-300.53, 192.6) * mm});
            skLineSegment(sketch, "E1004", {"start": v(-300.53, 192.6) * mm, "end": v(-306.07, 202.14) * mm});
            skArc(sketch, "E1005", {"start": v(-79.71, 204.22) * mm, "mid": v(-76.74, 208.4) * mm, "end": v(-80.57, 211.82) * mm});
            skArc(sketch, "E1006", {"start": v(-79.51, 202.22) * mm, "mid": v(-74.74, 208.5) * mm, "end": v(-80.57, 213.82) * mm});
            skLineSegment(sketch, "E1007", {"start": v(-80.57, 213.82) * mm, "end": v(-89, 213.82) * mm});
            skLineSegment(sketch, "E1008", {"start": v(-89, 213.82) * mm, "end": v(-89, 211.82) * mm});
            skLineSegment(sketch, "E1009", {"start": v(-89, 211.82) * mm, "end": v(-80.57, 211.82) * mm});
            skLineSegment(sketch, "E1010", {"start": v(-79.71, 204.22) * mm, "end": v(-89, 204.22) * mm});
            skLineSegment(sketch, "E1011", {"start": v(-89, 204.22) * mm, "end": v(-89, 192.82) * mm});
            skLineSegment(sketch, "E1012", {"start": v(-89, 192.82) * mm, "end": v(-87, 192.82) * mm});
            skLineSegment(sketch, "E1013", {"start": v(-87, 192.82) * mm, "end": v(-87, 202.22) * mm});
            skLineSegment(sketch, "E1014", {"start": v(-87, 202.22) * mm, "end": v(-81.51, 202.22) * mm});
            skLineSegment(sketch, "E1015", {"start": v(-81.51, 202.22) * mm, "end": v(-76.25, 192.69) * mm});
            skLineSegment(sketch, "E1016", {"start": v(-76.25, 192.69) * mm, "end": v(-73.97, 192.69) * mm});
            skLineSegment(sketch, "E1017", {"start": v(-73.97, 192.69) * mm, "end": v(-79.51, 202.22) * mm});
            skArc(sketch, "E1018", {"start": v(-306.27, 38.7) * mm, "mid": v(-303.3, 42.9) * mm, "end": v(-307.13, 46.31) * mm});
            skArc(sketch, "E1019", {"start": v(-306.07, 36.7) * mm, "mid": v(-301.3, 43) * mm, "end": v(-307.13, 48.31) * mm});
            skLineSegment(sketch, "E1020", {"start": v(-307.13, 48.31) * mm, "end": v(-315.57, 48.31) * mm});
            skLineSegment(sketch, "E1021", {"start": v(-315.57, 48.31) * mm, "end": v(-315.57, 46.31) * mm});
            skLineSegment(sketch, "E1022", {"start": v(-315.57, 46.31) * mm, "end": v(-307.13, 46.31) * mm});
            skLineSegment(sketch, "E1023", {"start": v(-306.27, 38.7) * mm, "end": v(-315.57, 38.7) * mm});
            skLineSegment(sketch, "E1024", {"start": v(-315.57, 38.7) * mm, "end": v(-315.57, 27.3) * mm});
            skLineSegment(sketch, "E1025", {"start": v(-315.57, 27.3) * mm, "end": v(-313.57, 27.3) * mm});
            skLineSegment(sketch, "E1026", {"start": v(-313.57, 27.3) * mm, "end": v(-313.57, 36.7) * mm});
            skLineSegment(sketch, "E1027", {"start": v(-313.57, 36.7) * mm, "end": v(-308.07, 36.7) * mm});
            skLineSegment(sketch, "E1028", {"start": v(-308.07, 36.7) * mm, "end": v(-302.8, 27.17) * mm});
            skLineSegment(sketch, "E1029", {"start": v(-302.8, 27.17) * mm, "end": v(-300.53, 27.17) * mm});
            skLineSegment(sketch, "E1030", {"start": v(-300.53, 27.17) * mm, "end": v(-306.07, 36.7) * mm});
            skArc(sketch, "E1031", {"start": v(33.44, 38.67) * mm, "mid": v(36.41, 42.86) * mm, "end": v(32.59, 46.28) * mm});
            skArc(sketch, "E1032", {"start": v(33.65, 36.67) * mm, "mid": v(38.41, 42.96) * mm, "end": v(32.59, 48.28) * mm});
            skLineSegment(sketch, "E1033", {"start": v(32.59, 48.28) * mm, "end": v(24.15, 48.28) * mm});
            skLineSegment(sketch, "E1034", {"start": v(24.15, 48.28) * mm, "end": v(24.15, 46.28) * mm});
            skLineSegment(sketch, "E1035", {"start": v(24.15, 46.28) * mm, "end": v(32.59, 46.28) * mm});
            skLineSegment(sketch, "E1036", {"start": v(33.44, 38.67) * mm, "end": v(24.15, 38.67) * mm});
            skLineSegment(sketch, "E1037", {"start": v(24.15, 38.67) * mm, "end": v(24.15, 27.27) * mm});
            skLineSegment(sketch, "E1038", {"start": v(24.15, 27.27) * mm, "end": v(26.15, 27.27) * mm});
            skLineSegment(sketch, "E1039", {"start": v(26.15, 27.27) * mm, "end": v(26.15, 36.67) * mm});
            skLineSegment(sketch, "E1040", {"start": v(26.15, 36.67) * mm, "end": v(31.65, 36.67) * mm});
            skLineSegment(sketch, "E1041", {"start": v(31.65, 36.67) * mm, "end": v(36.91, 27.14) * mm});
            skLineSegment(sketch, "E1042", {"start": v(36.91, 27.14) * mm, "end": v(39.19, 27.14) * mm});
            skLineSegment(sketch, "E1043", {"start": v(39.19, 27.14) * mm, "end": v(33.65, 36.67) * mm});
            skArc(sketch, "E1044", {"start": v(33.73, -85.97) * mm, "mid": v(36.7, -81.78) * mm, "end": v(32.87, -78.36) * mm});
            skArc(sketch, "E1045", {"start": v(33.93, -87.97) * mm, "mid": v(38.7, -81.68) * mm, "end": v(32.87, -76.36) * mm});
            skLineSegment(sketch, "E1046", {"start": v(32.87, -76.36) * mm, "end": v(24.43, -76.36) * mm});
            skLineSegment(sketch, "E1047", {"start": v(24.43, -76.36) * mm, "end": v(24.43, -78.36) * mm});
            skLineSegment(sketch, "E1048", {"start": v(24.43, -78.36) * mm, "end": v(32.87, -78.36) * mm});
            skLineSegment(sketch, "E1049", {"start": v(33.73, -85.97) * mm, "end": v(24.43, -85.97) * mm});
            skLineSegment(sketch, "E1050", {"start": v(24.43, -85.97) * mm, "end": v(24.43, -97.36) * mm});
            skLineSegment(sketch, "E1051", {"start": v(24.43, -97.36) * mm, "end": v(26.43, -97.36) * mm});
            skLineSegment(sketch, "E1052", {"start": v(26.43, -97.36) * mm, "end": v(26.43, -87.97) * mm});
            skLineSegment(sketch, "E1053", {"start": v(26.43, -87.97) * mm, "end": v(31.93, -87.97) * mm});
            skLineSegment(sketch, "E1054", {"start": v(31.93, -87.97) * mm, "end": v(37.2, -97.5) * mm});
            skLineSegment(sketch, "E1055", {"start": v(37.2, -97.5) * mm, "end": v(39.47, -97.5) * mm});
            skLineSegment(sketch, "E1056", {"start": v(39.47, -97.5) * mm, "end": v(33.93, -87.97) * mm});
            skLineSegment(sketch, "E1057", {"start": v(-90.33, 47.46) * mm, "end": v(-83.38, 26.77) * mm});
            skLineSegment(sketch, "E1058", {"start": v(-83.38, 26.77) * mm, "end": v(-81.4, 26.77) * mm});
            skLineSegment(sketch, "E1059", {"start": v(-81.4, 26.77) * mm, "end": v(-74.46, 47.46) * mm});
            skLineSegment(sketch, "E1060", {"start": v(-74.46, 47.46) * mm, "end": v(-76.57, 47.46) * mm});
            skLineSegment(sketch, "E1061", {"start": v(-76.57, 47.46) * mm, "end": v(-82.4, 30.12) * mm});
            skLineSegment(sketch, "E1062", {"start": v(-82.4, 30.12) * mm, "end": v(-88.22, 47.46) * mm});
            skLineSegment(sketch, "E1063", {"start": v(-88.22, 47.46) * mm, "end": v(-90.33, 47.46) * mm});
            skLineSegment(sketch, "E1064", {"start": v(-203.55, 213.51) * mm, "end": v(-196.6, 192.83) * mm});
            skLineSegment(sketch, "E1065", {"start": v(-196.6, 192.83) * mm, "end": v(-194.63, 192.83) * mm});
            skLineSegment(sketch, "E1066", {"start": v(-194.63, 192.83) * mm, "end": v(-187.68, 213.51) * mm});
            skLineSegment(sketch, "E1067", {"start": v(-187.68, 213.51) * mm, "end": v(-189.79, 213.51) * mm});
            skLineSegment(sketch, "E1068", {"start": v(-189.79, 213.51) * mm, "end": v(-195.62, 196.17) * mm});
            skLineSegment(sketch, "E1069", {"start": v(-195.62, 196.17) * mm, "end": v(-201.44, 213.51) * mm});
            skLineSegment(sketch, "E1070", {"start": v(-201.44, 213.51) * mm, "end": v(-203.55, 213.51) * mm});
            skLineSegment(sketch, "E1071", {"start": v(25.29, 192.83) * mm, "end": v(38.2, 192.83) * mm});
            skLineSegment(sketch, "E1072", {"start": v(38.2, 192.83) * mm, "end": v(38.2, 194.83) * mm});
            skLineSegment(sketch, "E1073", {"start": v(38.2, 194.83) * mm, "end": v(27.29, 194.83) * mm});
            skLineSegment(sketch, "E1074", {"start": v(27.29, 194.83) * mm, "end": v(27.29, 214.2) * mm});
            skLineSegment(sketch, "E1075", {"start": v(27.29, 214.2) * mm, "end": v(25.29, 214.2) * mm});
            skLineSegment(sketch, "E1076", {"start": v(25.29, 214.2) * mm, "end": v(25.29, 192.83) * mm});
            skLineSegment(sketch, "E1077", {"start": v(-125.35, 109.65) * mm, "end": v(-112.43, 109.65) * mm});
            skLineSegment(sketch, "E1078", {"start": v(-112.43, 109.65) * mm, "end": v(-112.43, 111.65) * mm});
            skLineSegment(sketch, "E1079", {"start": v(-112.43, 111.65) * mm, "end": v(-123.35, 111.65) * mm});
            skLineSegment(sketch, "E1080", {"start": v(-123.35, 111.65) * mm, "end": v(-123.35, 131.03) * mm});
            skLineSegment(sketch, "E1081", {"start": v(-123.35, 131.03) * mm, "end": v(-125.35, 131.03) * mm});
            skLineSegment(sketch, "E1082", {"start": v(-125.35, 131.03) * mm, "end": v(-125.35, 109.65) * mm});
            skLineSegment(sketch, "E1083", {"start": v(-125.35, -14.58) * mm, "end": v(-112.43, -14.58) * mm});
            skLineSegment(sketch, "E1084", {"start": v(-112.43, -14.58) * mm, "end": v(-112.43, -12.58) * mm});
            skLineSegment(sketch, "E1085", {"start": v(-112.43, -12.58) * mm, "end": v(-123.35, -12.58) * mm});
            skLineSegment(sketch, "E1086", {"start": v(-123.35, -12.58) * mm, "end": v(-123.35, 6.8) * mm});
            skLineSegment(sketch, "E1087", {"start": v(-123.35, 6.8) * mm, "end": v(-125.35, 6.8) * mm});
            skLineSegment(sketch, "E1088", {"start": v(-125.35, 6.8) * mm, "end": v(-125.35, -14.58) * mm});
            skLineSegment(sketch, "E1089", {"start": v(-12.14, -55.41) * mm, "end": v(0.78, -55.41) * mm});
            skLineSegment(sketch, "E1090", {"start": v(0.78, -55.41) * mm, "end": v(0.78, -53.41) * mm});
            skLineSegment(sketch, "E1091", {"start": v(0.78, -53.41) * mm, "end": v(-10.14, -53.41) * mm});
            skLineSegment(sketch, "E1092", {"start": v(-10.14, -53.41) * mm, "end": v(-10.14, -34.03) * mm});
            skLineSegment(sketch, "E1093", {"start": v(-10.14, -34.03) * mm, "end": v(-12.14, -34.03) * mm});
            skLineSegment(sketch, "E1094", {"start": v(-12.14, -34.03) * mm, "end": v(-12.14, -55.41) * mm});
            skLineSegment(sketch, "E1095", {"start": v(-166.89, 26.82) * mm, "end": v(-166.89, 48.14) * mm});
            skLineSegment(sketch, "E1096", {"start": v(-166.89, 48.14) * mm, "end": v(-165.4, 48.14) * mm});
            skLineSegment(sketch, "E1097", {"start": v(-165.4, 48.14) * mm, "end": v(-157.9, 32.88) * mm});
            skLineSegment(sketch, "E1098", {"start": v(-157.9, 32.88) * mm, "end": v(-150.88, 48.14) * mm});
            skLineSegment(sketch, "E1099", {"start": v(-150.88, 48.14) * mm, "end": v(-149.25, 48.14) * mm});
            skLineSegment(sketch, "E1100", {"start": v(-149.25, 48.14) * mm, "end": v(-149.25, 26.82) * mm});
            skLineSegment(sketch, "E1101", {"start": v(-149.25, 26.82) * mm, "end": v(-151.25, 26.82) * mm});
            skLineSegment(sketch, "E1102", {"start": v(-151.25, 26.82) * mm, "end": v(-151.25, 42.55) * mm});
            skLineSegment(sketch, "E1103", {"start": v(-151.25, 42.55) * mm, "end": v(-157.04, 29.98) * mm});
            skLineSegment(sketch, "E1104", {"start": v(-157.04, 29.98) * mm, "end": v(-158.71, 29.98) * mm});
            skLineSegment(sketch, "E1105", {"start": v(-158.71, 29.98) * mm, "end": v(-164.89, 42.55) * mm});
            skLineSegment(sketch, "E1106", {"start": v(-164.89, 42.55) * mm, "end": v(-164.89, 26.82) * mm});
            skLineSegment(sketch, "E1107", {"start": v(-164.89, 26.82) * mm, "end": v(-166.89, 26.82) * mm});
            skLineSegment(sketch, "E1108", {"start": v(-276.33, -0.8) * mm, "end": v(-276.33, -7.95) * mm});
            skLineSegment(sketch, "E1109", {"start": v(-278.33, -7.95) * mm, "end": v(-278.33, -0.8) * mm});
            skArc(sketch, "E1110", {"start": v(-276.33, -0.8) * mm, "mid": v(-271.29, 4.43) * mm, "end": v(-265.86, -0.42) * mm});
            skArc(sketch, "E1111", {"start": v(-278.33, -0.8) * mm, "mid": v(-271.29, 6.43) * mm, "end": v(-263.86, -0.42) * mm});
            skArc(sketch, "E1112", {"start": v(-276.33, -7.95) * mm, "mid": v(-271.4, -13.2) * mm, "end": v(-265.86, -8.6) * mm});
            skArc(sketch, "E1113", {"start": v(-278.33, -7.95) * mm, "mid": v(-271.4, -15.2) * mm, "end": v(-263.86, -8.6) * mm});
            skLineSegment(sketch, "E1114", {"start": v(-265.86, -8.6) * mm, "end": v(-263.86, -8.6) * mm});
            skLineSegment(sketch, "E1115", {"start": v(-265.86, -0.42) * mm, "end": v(-263.86, -0.42) * mm});
            skLineSegment(sketch, "E1116", {"start": v(-49.62, -0.29) * mm, "end": v(-49.62, -7.43) * mm});
            skLineSegment(sketch, "E1117", {"start": v(-51.62, -7.43) * mm, "end": v(-51.62, -0.29) * mm});
            skArc(sketch, "E1118", {"start": v(-49.62, -0.29) * mm, "mid": v(-44.58, 4.95) * mm, "end": v(-39.16, 0.1) * mm});
            skArc(sketch, "E1119", {"start": v(-51.62, -0.29) * mm, "mid": v(-44.58, 6.95) * mm, "end": v(-37.16, 0.1) * mm});
            skArc(sketch, "E1120", {"start": v(-49.62, -7.43) * mm, "mid": v(-44.7, -12.67) * mm, "end": v(-39.16, -8.08) * mm});
            skArc(sketch, "E1121", {"start": v(-51.62, -7.43) * mm, "mid": v(-44.7, -14.67) * mm, "end": v(-37.16, -8.08) * mm});
            skLineSegment(sketch, "E1122", {"start": v(-39.16, -8.08) * mm, "end": v(-37.16, -8.08) * mm});
            skLineSegment(sketch, "E1123", {"start": v(-39.16, 0.1) * mm, "end": v(-37.16, 0.1) * mm});
            skLineSegment(sketch, "E1124", {"start": v(-14.14, -14.49) * mm, "end": v(-14.14, 6.9) * mm});
            skLineSegment(sketch, "E1125", {"start": v(-14.14, 6.9) * mm, "end": v(-12.14, 6.9) * mm});
            skLineSegment(sketch, "E1126", {"start": v(-12.14, 6.9) * mm, "end": v(-12.14, -2.78) * mm});
            skLineSegment(sketch, "E1127", {"start": v(-12.14, -2.78) * mm, "end": v(-1.94, -2.78) * mm});
            skLineSegment(sketch, "E1128", {"start": v(-1.94, -2.78) * mm, "end": v(-1.94, 6.9) * mm});
            skLineSegment(sketch, "E1129", {"start": v(-1.94, 6.9) * mm, "end": v(0.06, 6.9) * mm});
            skLineSegment(sketch, "E1130", {"start": v(0.06, 6.9) * mm, "end": v(0.06, -14.49) * mm});
            skLineSegment(sketch, "E1131", {"start": v(0.06, -14.49) * mm, "end": v(-1.94, -14.49) * mm});
            skLineSegment(sketch, "E1132", {"start": v(-1.94, -14.49) * mm, "end": v(-1.94, -4.78) * mm});
            skLineSegment(sketch, "E1133", {"start": v(-1.94, -4.78) * mm, "end": v(-12.14, -4.78) * mm});
            skLineSegment(sketch, "E1134", {"start": v(-12.14, -4.78) * mm, "end": v(-12.14, -14.49) * mm});
            skLineSegment(sketch, "E1135", {"start": v(-12.14, -14.49) * mm, "end": v(-14.14, -14.49) * mm});
            skLineSegment(sketch, "E1136", {"start": v(-165.17, -76.6) * mm, "end": v(-165.17, -91.3) * mm});
            skLineSegment(sketch, "E1137", {"start": v(-163.17, -76.6) * mm, "end": v(-163.17, -91.3) * mm});
            skLineSegment(sketch, "E1138", {"start": v(-165.17, -76.6) * mm, "end": v(-163.17, -76.6) * mm});
            skLineSegment(sketch, "E1139", {"start": v(-152.98, -76.6) * mm, "end": v(-152.98, -91.3) * mm});
            skLineSegment(sketch, "E1140", {"start": v(-150.98, -76.6) * mm, "end": v(-150.98, -91.3) * mm});
            skLineSegment(sketch, "E1141", {"start": v(-152.98, -76.6) * mm, "end": v(-150.98, -76.6) * mm});
            skArc(sketch, "E1142", {"start": v(-163.17, -91.3) * mm, "mid": v(-158.07, -96.4) * mm, "end": v(-152.98, -91.3) * mm});
            skArc(sketch, "E1143", {"start": v(-165.17, -91.3) * mm, "mid": v(-158.07, -98.4) * mm, "end": v(-150.98, -91.3) * mm});
            skLineSegment(sketch, "E1144", {"start": v(-51.82, -75.7) * mm, "end": v(-51.82, -90.4) * mm});
            skLineSegment(sketch, "E1145", {"start": v(-49.82, -75.7) * mm, "end": v(-49.82, -90.4) * mm});
            skLineSegment(sketch, "E1146", {"start": v(-51.82, -75.7) * mm, "end": v(-49.82, -75.7) * mm});
            skLineSegment(sketch, "E1147", {"start": v(-39.63, -75.7) * mm, "end": v(-39.63, -90.4) * mm});
            skLineSegment(sketch, "E1148", {"start": v(-37.63, -75.7) * mm, "end": v(-37.63, -90.4) * mm});
            skLineSegment(sketch, "E1149", {"start": v(-39.63, -75.7) * mm, "end": v(-37.63, -75.7) * mm});
            skArc(sketch, "E1150", {"start": v(-49.82, -90.4) * mm, "mid": v(-44.73, -95.5) * mm, "end": v(-39.63, -90.4) * mm});
            skArc(sketch, "E1151", {"start": v(-51.82, -90.4) * mm, "mid": v(-44.73, -97.5) * mm, "end": v(-37.63, -90.4) * mm});
            skLineSegment(sketch, "E1152", {"start": v(-240.27, -35.05) * mm, "end": v(-238.27, -35.05) * mm});
            skLineSegment(sketch, "E1153", {"start": v(-238.27, -35.05) * mm, "end": v(-238.27, -54.01) * mm});
            skLineSegment(sketch, "E1154", {"start": v(-238.27, -54.01) * mm, "end": v(-232.05, -54.01) * mm});
            skLineSegment(sketch, "E1155", {"start": v(-240.27, -35.05) * mm, "end": v(-240.27, -56.01) * mm});
            skLineSegment(sketch, "E1156", {"start": v(-240.27, -56.01) * mm, "end": v(-232.05, -56.01) * mm});
            skArc(sketch, "E1157", {"start": v(-232.05, -54.01) * mm, "mid": v(-228.06, -50.02) * mm, "end": v(-232.05, -46.03) * mm});
            skArc(sketch, "E1158", {"start": v(-232.05, -56.01) * mm, "mid": v(-226.37, -51.65) * mm, "end": v(-229.11, -45.04) * mm});
            skLineSegment(sketch, "E1159", {"start": v(-232.05, -46.03) * mm, "end": v(-235.96, -46.03) * mm});
            skLineSegment(sketch, "E1160", {"start": v(-235.96, -46.03) * mm, "end": v(-235.96, -44.03) * mm});
            skLineSegment(sketch, "E1161", {"start": v(-235.96, -44.03) * mm, "end": v(-232.05, -44.03) * mm});
            skArc(sketch, "E1162", {"start": v(-232.05, -44.03) * mm, "mid": v(-228.55, -40.54) * mm, "end": v(-232.05, -37.05) * mm});
            skLineSegment(sketch, "E1163", {"start": v(-232.05, -37.05) * mm, "end": v(-235.96, -37.05) * mm});
            skLineSegment(sketch, "E1164", {"start": v(-235.96, -37.05) * mm, "end": v(-235.96, -35.05) * mm});
            skLineSegment(sketch, "E1165", {"start": v(-235.96, -35.05) * mm, "end": v(-232.05, -35.05) * mm});
            skArc(sketch, "E1166", {"start": v(-232.05, -35.05) * mm, "mid": v(-226.84, -38.95) * mm, "end": v(-229.11, -45.04) * mm});
            skLineSegment(sketch, "E1167", {"start": v(-39.5, 296.68) * mm, "end": v(-39.5, 282.44) * mm});
            skSolve(sketch);
        }
        {
            var Q0;
            Q0 = qSketchRegion(id + "F0", true);
            extrude(context, id + "F1", {"entities" : qUnion([Q0]), "depth" : 2 * mm});
        }
    });
